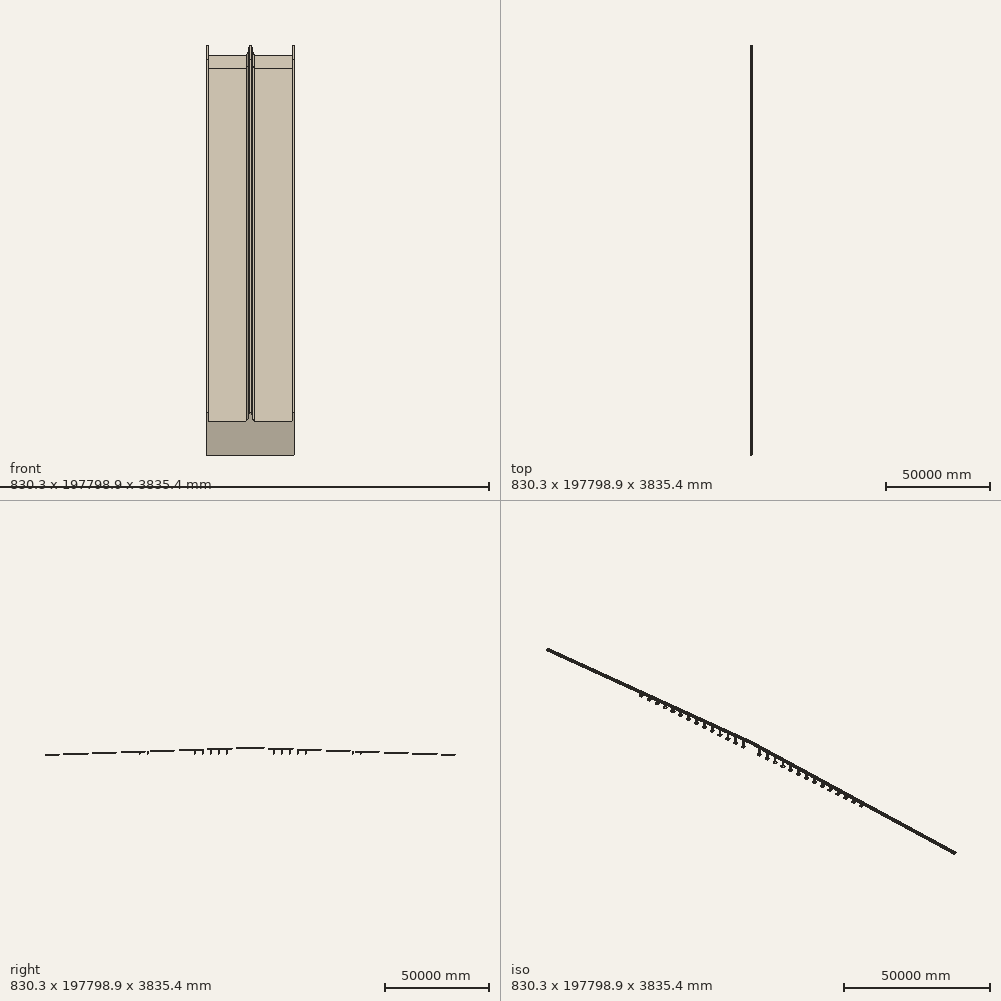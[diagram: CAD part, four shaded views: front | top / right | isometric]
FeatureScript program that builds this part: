
annotation { "Feature Type Name" : "Feature", "Feature Type Description" : "" }
export const myFeature = defineFeature(function(context is Context, id is Id, definition is map)
    precondition{}
    {
        {
            var Q0;
            Q0=qCreatedBy(makeId("Front.planeOp"),FACE);
            var sketch = newSketch(context, id + "F0", { "sketchPlane" : qUnion([Q0])});
            skLineSegment(sketch, "E0", {"start": v(-12.7, 88.9) * mm, "end": v(12.7, 88.9) * mm});
            skLineSegment(sketch, "E1", {"start": v(12.7, 88.9) * mm, "end": v(16.93, 27.52) * mm});
            skLineSegment(sketch, "E2", {"start": v(16.93, 27.52) * mm, "end": v(34.13, 6.35) * mm});
            skLineSegment(sketch, "E3", {"start": v(34.13, 6.35) * mm, "end": v(34.13, 0) * mm});
            skPoint(sketch, "E4", {"position": v(0, 88.9) * mm});
            skLineSegment(sketch, "E5", {"start": v(0, 0) * mm, "end": v(0, 88.9) * mm, "construction": true});
            skLineSegment(sketch, "E6.MirrorCS", {"start": v(-12.7, 88.9) * mm, "end": v(-16.93, 27.52) * mm});
            skLineSegment(sketch, "E7.MirrorCS", {"start": v(-16.93, 27.52) * mm, "end": v(-34.13, 6.35) * mm});
            skLineSegment(sketch, "E8.MirrorCS", {"start": v(-34.13, 6.35) * mm, "end": v(-34.13, 0) * mm});
            skLineSegment(sketch, "E9", {"start": v(34.13, 0) * mm, "end": v(389.73, 0) * mm});
            skLineSegment(sketch, "E10", {"start": v(389.73, 0) * mm, "end": v(389.73, 88.9) * mm});
            skLineSegment(sketch, "E11", {"start": v(389.73, 88.9) * mm, "end": v(415.13, 88.9) * mm});
            skLineSegment(sketch, "E12", {"start": v(415.13, 88.9) * mm, "end": v(415.13, -317.5) * mm});
            skLineSegment(sketch, "E13.MirrorCS", {"start": v(-34.13, 0) * mm, "end": v(-389.73, 0) * mm});
            skLineSegment(sketch, "E14.MirrorCS", {"start": v(-389.73, 0) * mm, "end": v(-389.73, 88.9) * mm});
            skLineSegment(sketch, "E15.MirrorCS", {"start": v(-389.73, 88.9) * mm, "end": v(-415.13, 88.9) * mm});
            skLineSegment(sketch, "E16.MirrorCS", {"start": v(-415.13, 88.9) * mm, "end": v(-415.13, -317.5) * mm});
            skLineSegment(sketch, "E17", {"start": v(-415.13, -317.5) * mm, "end": v(415.13, -317.5) * mm});
            skSolve(sketch);
        }
        {
            var Q0;
            Q0=qCreatedBy(makeId("Right.planeOp"),FACE);
            var sketch = newSketch(context, id + "F1", { "sketchPlane" : qUnion([Q0])});
            skLineSegment(sketch, "E18", {"start": v(0, -317.5) * mm, "end": v(0, -3746.5) * mm, "construction": true});
            skLineSegment(sketch, "E19", {"start": v(-98885.1, -3746.5) * mm, "end": v(-3628.85, -443.34) * mm});
            skPoint(sketch, "E20.visualSharp", {"position": v(0, -317.5) * mm});
            skArc(sketch, "E21", {"start": v(0, -317.5) * mm, "mid": v(-1815.54, -348.33) * mm, "end": v(-3628.85, -443.34) * mm});
            skSolve(sketch);
        }
        {
            var Q0;
            Q0 = qSketchRegion(id + "F0", true);
            var Q1;
            Q1 = qConstructionFilter(qBodyType(qCreatedBy(id + "F1" ,EDGE), BodyType.WIRE), ConstructionObject.NO);
            sweep(context, id + "F2", {"profiles" : qUnion([Q0]), "path" : qUnion([Q1])});
        }
        {
            var Q0;
            Q0=makeQuery(id+"F2.opSweep","SWEPT_BODY",BODY,{"disambiguationData":[OSD([sQuery(id+"F0.wireOp",EDGE,"E0"),sQuery(id+"F0.wireOp",EDGE,"E1"),sQuery(id+"F0.wireOp",EDGE,"E2"),sQuery(id+"F0.wireOp",EDGE,"E3"),sQuery(id+"F0.wireOp",EDGE,"E6.MirrorCS"),sQuery(id+"F0.wireOp",EDGE,"E7.MirrorCS"),sQuery(id+"F0.wireOp",EDGE,"E8.MirrorCS"),sQuery(id+"F0.wireOp",EDGE,"E9"),sQuery(id+"F0.wireOp",EDGE,"E10"),sQuery(id+"F0.wireOp",EDGE,"E11"),sQuery(id+"F0.wireOp",EDGE,"E12"),sQuery(id+"F0.wireOp",EDGE,"E13.MirrorCS"),sQuery(id+"F0.wireOp",EDGE,"E14.MirrorCS"),sQuery(id+"F0.wireOp",EDGE,"E15.MirrorCS"),sQuery(id+"F0.wireOp",EDGE,"E16.MirrorCS"),sQuery(id+"F0.wireOp",EDGE,"E17"),sQuery(id+"F1.wireOp",EDGE,"E21")])]});
            var Q1;
            Q1=qCreatedBy(makeId("Front.planeOp"),FACE);
            mirror(context, id + "F3", {"operationType" : NewBodyOperationType.ADD, "entities" : qUnion([Q0]), "mirrorPlane" : qUnion([Q1])});
        }
        {
            var Q0;
            Q0=qCreatedBy(makeId("Top.planeOp"),FACE);
            cPlane(context, id + "F4", {"entities" : qUnion([Q0]), "cplaneType" : CPlaneType.OFFSET, "offset" : 3429 * mm, "oppositeDirection" : true, "width" : 152.4 * mm, "height" : 152.4 * mm});
        }
        {
            var Q0;
            Q0=qCreatedBy(id+"F4.planeOp",FACE);
            var sketch = newSketch(context, id + "F5", { "sketchPlane" : qUnion([Q0])});
            skLineSegment(sketch, "E22.bottom", {"start": v(-415.13, 3175) * mm, "end": v(415.13, 3175) * mm});
            skLineSegment(sketch, "E22.top", {"start": v(-415.13, 4445) * mm, "end": v(415.13, 4445) * mm});
            skLineSegment(sketch, "E22.left", {"start": v(-415.13, 3175) * mm, "end": v(-415.13, 4445) * mm});
            skLineSegment(sketch, "E22.right", {"start": v(415.13, 3175) * mm, "end": v(415.13, 4445) * mm});
            skLineSegment(sketch, "E23.0.1.0", {"start": v(415.13, 6985) * mm, "end": v(415.13, 8255) * mm});
            skLineSegment(sketch, "E23.0.1.1", {"start": v(-415.13, 6985) * mm, "end": v(-415.13, 8255) * mm});
            skLineSegment(sketch, "E23.0.1.2", {"start": v(-415.13, 8255) * mm, "end": v(415.13, 8255) * mm});
            skLineSegment(sketch, "E23.0.1.3", {"start": v(-415.13, 6985) * mm, "end": v(415.13, 6985) * mm});
            skLineSegment(sketch, "E23.0.2.0", {"start": v(415.13, 10795) * mm, "end": v(415.13, 12065) * mm});
            skLineSegment(sketch, "E23.0.2.1", {"start": v(-415.13, 10795) * mm, "end": v(-415.13, 12065) * mm});
            skLineSegment(sketch, "E23.0.2.2", {"start": v(-415.13, 12065) * mm, "end": v(415.13, 12065) * mm});
            skLineSegment(sketch, "E23.0.2.3", {"start": v(-415.13, 10795) * mm, "end": v(415.13, 10795) * mm});
            skLineSegment(sketch, "E23.0.3.0", {"start": v(415.13, 14605) * mm, "end": v(415.13, 15875) * mm});
            skLineSegment(sketch, "E23.0.3.1", {"start": v(-415.13, 14605) * mm, "end": v(-415.13, 15875) * mm});
            skLineSegment(sketch, "E23.0.3.2", {"start": v(-415.13, 15875) * mm, "end": v(415.13, 15875) * mm});
            skLineSegment(sketch, "E23.0.3.3", {"start": v(-415.13, 14605) * mm, "end": v(415.13, 14605) * mm});
            skLineSegment(sketch, "E23.0.4.0", {"start": v(415.13, 18415) * mm, "end": v(415.13, 19685) * mm});
            skLineSegment(sketch, "E23.0.4.1", {"start": v(-415.13, 18415) * mm, "end": v(-415.13, 19685) * mm});
            skLineSegment(sketch, "E23.0.4.2", {"start": v(-415.13, 19685) * mm, "end": v(415.13, 19685) * mm});
            skLineSegment(sketch, "E23.0.4.3", {"start": v(-415.13, 18415) * mm, "end": v(415.13, 18415) * mm});
            skLineSegment(sketch, "E23.0.5.0", {"start": v(415.13, 22225) * mm, "end": v(415.13, 23495) * mm});
            skLineSegment(sketch, "E23.0.5.1", {"start": v(-415.13, 22225) * mm, "end": v(-415.13, 23495) * mm});
            skLineSegment(sketch, "E23.0.5.2", {"start": v(-415.13, 23495) * mm, "end": v(415.13, 23495) * mm});
            skLineSegment(sketch, "E23.0.5.3", {"start": v(-415.13, 22225) * mm, "end": v(415.13, 22225) * mm});
            skLineSegment(sketch, "E23.0.6.0", {"start": v(415.13, 26035) * mm, "end": v(415.13, 27305) * mm});
            skLineSegment(sketch, "E23.0.6.1", {"start": v(-415.13, 26035) * mm, "end": v(-415.13, 27305) * mm});
            skLineSegment(sketch, "E23.0.6.2", {"start": v(-415.13, 27305) * mm, "end": v(415.13, 27305) * mm});
            skLineSegment(sketch, "E23.0.6.3", {"start": v(-415.13, 26035) * mm, "end": v(415.13, 26035) * mm});
            skLineSegment(sketch, "E23.0.7.0", {"start": v(415.13, 29845) * mm, "end": v(415.13, 31115) * mm});
            skLineSegment(sketch, "E23.0.7.1", {"start": v(-415.13, 29845) * mm, "end": v(-415.13, 31115) * mm});
            skLineSegment(sketch, "E23.0.7.2", {"start": v(-415.13, 31115) * mm, "end": v(415.13, 31115) * mm});
            skLineSegment(sketch, "E23.0.7.3", {"start": v(-415.13, 29845) * mm, "end": v(415.13, 29845) * mm});
            skLineSegment(sketch, "E23.direction1", {"start": v(-415.13, 3175) * mm, "end": v(-389.73, 3175) * mm, "construction": true});
            skLineSegment(sketch, "E23.direction2", {"start": v(-415.13, 3175) * mm, "end": v(-415.13, 6985) * mm, "construction": true});
            skLineSegment(sketch, "E24.0.0.8", {"start": v(415.13, 33655) * mm, "end": v(415.13, 34925) * mm});
            skLineSegment(sketch, "E24.3.0.8", {"start": v(-415.13, 33655) * mm, "end": v(-415.13, 34925) * mm});
            skLineSegment(sketch, "E24.6.0.8", {"start": v(-415.13, 34925) * mm, "end": v(415.13, 34925) * mm});
            skLineSegment(sketch, "E24.9.0.8", {"start": v(-415.13, 33655) * mm, "end": v(415.13, 33655) * mm});
            skLineSegment(sketch, "E24.0.0.9", {"start": v(415.13, 37465) * mm, "end": v(415.13, 38735) * mm});
            skLineSegment(sketch, "E24.3.0.9", {"start": v(-415.13, 37465) * mm, "end": v(-415.13, 38735) * mm});
            skLineSegment(sketch, "E24.6.0.9", {"start": v(-415.13, 38735) * mm, "end": v(415.13, 38735) * mm});
            skLineSegment(sketch, "E24.9.0.9", {"start": v(-415.13, 37465) * mm, "end": v(415.13, 37465) * mm});
            skLineSegment(sketch, "E24.0.0.10", {"start": v(415.13, 41275) * mm, "end": v(415.13, 42545) * mm});
            skLineSegment(sketch, "E24.3.0.10", {"start": v(-415.13, 41275) * mm, "end": v(-415.13, 42545) * mm});
            skLineSegment(sketch, "E24.6.0.10", {"start": v(-415.13, 42545) * mm, "end": v(415.13, 42545) * mm});
            skLineSegment(sketch, "E24.9.0.10", {"start": v(-415.13, 41275) * mm, "end": v(415.13, 41275) * mm});
            skLineSegment(sketch, "E24.0.0.11", {"start": v(415.13, 45085) * mm, "end": v(415.13, 46355) * mm});
            skLineSegment(sketch, "E24.3.0.11", {"start": v(-415.13, 45085) * mm, "end": v(-415.13, 46355) * mm});
            skLineSegment(sketch, "E24.6.0.11", {"start": v(-415.13, 46355) * mm, "end": v(415.13, 46355) * mm});
            skLineSegment(sketch, "E24.9.0.11", {"start": v(-415.13, 45085) * mm, "end": v(415.13, 45085) * mm});
            skLineSegment(sketch, "E24.0.0.12", {"start": v(415.13, 48895) * mm, "end": v(415.13, 50165) * mm});
            skLineSegment(sketch, "E24.3.0.12", {"start": v(-415.13, 48895) * mm, "end": v(-415.13, 50165) * mm});
            skLineSegment(sketch, "E24.6.0.12", {"start": v(-415.13, 50165) * mm, "end": v(415.13, 50165) * mm});
            skLineSegment(sketch, "E24.9.0.12", {"start": v(-415.13, 48895) * mm, "end": v(415.13, 48895) * mm});
            skLineSegment(sketch, "E24.0.0.13", {"start": v(415.13, 52705) * mm, "end": v(415.13, 53975) * mm});
            skLineSegment(sketch, "E24.3.0.13", {"start": v(-415.13, 52705) * mm, "end": v(-415.13, 53975) * mm});
            skLineSegment(sketch, "E24.6.0.13", {"start": v(-415.13, 53975) * mm, "end": v(415.13, 53975) * mm});
            skLineSegment(sketch, "E24.9.0.13", {"start": v(-415.13, 52705) * mm, "end": v(415.13, 52705) * mm});
            skLineSegment(sketch, "E25", {"start": v(-1571.05, 0) * mm, "end": v(1415.11, 0) * mm, "construction": true});
            skLineSegment(sketch, "E26.MirrorCS", {"start": v(-415.13, -3175) * mm, "end": v(415.13, -3175) * mm});
            skLineSegment(sketch, "E27.MirrorCS", {"start": v(-415.13, -3175) * mm, "end": v(-389.73, -3175) * mm, "construction": true});
            skLineSegment(sketch, "E28.MirrorCS", {"start": v(415.13, -6985) * mm, "end": v(415.13, -8255) * mm});
            skLineSegment(sketch, "E29.MirrorCS", {"start": v(-415.13, -6985) * mm, "end": v(-415.13, -8255) * mm});
            skLineSegment(sketch, "E30.MirrorCS", {"start": v(-415.13, -6985) * mm, "end": v(415.13, -6985) * mm});
            skLineSegment(sketch, "E31.MirrorCS", {"start": v(415.13, -52705) * mm, "end": v(415.13, -53975) * mm});
            skLineSegment(sketch, "E32.MirrorCS", {"start": v(-415.13, -19685) * mm, "end": v(415.13, -19685) * mm});
            skLineSegment(sketch, "E33.MirrorCS", {"start": v(415.13, -33655) * mm, "end": v(415.13, -34925) * mm});
            skLineSegment(sketch, "E34.MirrorCS", {"start": v(-415.13, -26035) * mm, "end": v(-415.13, -27305) * mm});
            skLineSegment(sketch, "E35.MirrorCS", {"start": v(-415.13, -37465) * mm, "end": v(415.13, -37465) * mm});
            skLineSegment(sketch, "E36.MirrorCS", {"start": v(-415.13, -52705) * mm, "end": v(415.13, -52705) * mm});
            skLineSegment(sketch, "E37.MirrorCS", {"start": v(-415.13, -18415) * mm, "end": v(-415.13, -19685) * mm});
            skLineSegment(sketch, "E38.MirrorCS", {"start": v(-415.13, -3175) * mm, "end": v(-415.13, -6985) * mm, "construction": true});
            skLineSegment(sketch, "E39.MirrorCS", {"start": v(-415.13, -45085) * mm, "end": v(-415.13, -46355) * mm});
            skLineSegment(sketch, "E40.MirrorCS", {"start": v(-415.13, -23495) * mm, "end": v(415.13, -23495) * mm});
            skLineSegment(sketch, "E41.MirrorCS", {"start": v(415.13, -26035) * mm, "end": v(415.13, -27305) * mm});
            skLineSegment(sketch, "E42.MirrorCS", {"start": v(-415.13, -38735) * mm, "end": v(415.13, -38735) * mm});
            skLineSegment(sketch, "E43.MirrorCS", {"start": v(-415.13, -53975) * mm, "end": v(415.13, -53975) * mm});
            skLineSegment(sketch, "E44.MirrorCS", {"start": v(-415.13, -45085) * mm, "end": v(415.13, -45085) * mm});
            skLineSegment(sketch, "E45.MirrorCS", {"start": v(-415.13, -22225) * mm, "end": v(415.13, -22225) * mm});
            skLineSegment(sketch, "E46.MirrorCS", {"start": v(-415.13, -37465) * mm, "end": v(-415.13, -38735) * mm});
            skLineSegment(sketch, "E47.MirrorCS", {"start": v(-415.13, -52705) * mm, "end": v(-415.13, -53975) * mm});
            skLineSegment(sketch, "E48.MirrorCS", {"start": v(-415.13, -29845) * mm, "end": v(415.13, -29845) * mm});
            skLineSegment(sketch, "E49.MirrorCS", {"start": v(415.13, -37465) * mm, "end": v(415.13, -38735) * mm});
            skLineSegment(sketch, "E50.MirrorCS", {"start": v(-415.13, -48895) * mm, "end": v(415.13, -48895) * mm});
            skLineSegment(sketch, "E51.MirrorCS", {"start": v(415.13, -45085) * mm, "end": v(415.13, -46355) * mm});
            skLineSegment(sketch, "E52.MirrorCS", {"start": v(-415.13, -22225) * mm, "end": v(-415.13, -23495) * mm});
            skLineSegment(sketch, "E53.MirrorCS", {"start": v(-415.13, -31115) * mm, "end": v(415.13, -31115) * mm});
            skLineSegment(sketch, "E54.MirrorCS", {"start": v(-415.13, -33655) * mm, "end": v(415.13, -33655) * mm});
            skLineSegment(sketch, "E55.MirrorCS", {"start": v(415.13, -14605) * mm, "end": v(415.13, -15875) * mm});
            skLineSegment(sketch, "E56.MirrorCS", {"start": v(-415.13, -10795) * mm, "end": v(415.13, -10795) * mm});
            skLineSegment(sketch, "E57.MirrorCS", {"start": v(415.13, -48895) * mm, "end": v(415.13, -50165) * mm});
            skLineSegment(sketch, "E58.MirrorCS", {"start": v(-415.13, -4445) * mm, "end": v(415.13, -4445) * mm});
            skLineSegment(sketch, "E59.MirrorCS", {"start": v(415.13, -22225) * mm, "end": v(415.13, -23495) * mm});
            skLineSegment(sketch, "E60.MirrorCS", {"start": v(-415.13, -34925) * mm, "end": v(415.13, -34925) * mm});
            skLineSegment(sketch, "E61.MirrorCS", {"start": v(-415.13, -14605) * mm, "end": v(415.13, -14605) * mm});
            skLineSegment(sketch, "E62.MirrorCS", {"start": v(-415.13, -18415) * mm, "end": v(415.13, -18415) * mm});
            skLineSegment(sketch, "E63.MirrorCS", {"start": v(-415.13, -3175) * mm, "end": v(-415.13, -4445) * mm});
            skLineSegment(sketch, "E64.MirrorCS", {"start": v(415.13, -3175) * mm, "end": v(415.13, -4445) * mm});
            skLineSegment(sketch, "E65.MirrorCS", {"start": v(-415.13, -48895) * mm, "end": v(-415.13, -50165) * mm});
            skLineSegment(sketch, "E66.MirrorCS", {"start": v(-415.13, -15875) * mm, "end": v(415.13, -15875) * mm});
            skLineSegment(sketch, "E67.MirrorCS", {"start": v(-415.13, -46355) * mm, "end": v(415.13, -46355) * mm});
            skLineSegment(sketch, "E68.MirrorCS", {"start": v(-415.13, -12065) * mm, "end": v(415.13, -12065) * mm});
            skLineSegment(sketch, "E69.MirrorCS", {"start": v(-415.13, -33655) * mm, "end": v(-415.13, -34925) * mm});
            skLineSegment(sketch, "E70.MirrorCS", {"start": v(-415.13, -42545) * mm, "end": v(415.13, -42545) * mm});
            skLineSegment(sketch, "E71.MirrorCS", {"start": v(415.13, -29845) * mm, "end": v(415.13, -31115) * mm});
            skLineSegment(sketch, "E72.MirrorCS", {"start": v(415.13, -41275) * mm, "end": v(415.13, -42545) * mm});
            skLineSegment(sketch, "E73.MirrorCS", {"start": v(-415.13, -27305) * mm, "end": v(415.13, -27305) * mm});
            skLineSegment(sketch, "E74.MirrorCS", {"start": v(-415.13, -29845) * mm, "end": v(-415.13, -31115) * mm});
            skLineSegment(sketch, "E75.MirrorCS", {"start": v(-415.13, -26035) * mm, "end": v(415.13, -26035) * mm});
            skLineSegment(sketch, "E76.MirrorCS", {"start": v(-415.13, -41275) * mm, "end": v(-415.13, -42545) * mm});
            skLineSegment(sketch, "E77.MirrorCS", {"start": v(-415.13, -14605) * mm, "end": v(-415.13, -15875) * mm});
            skLineSegment(sketch, "E78.MirrorCS", {"start": v(-415.13, -50165) * mm, "end": v(415.13, -50165) * mm});
            skLineSegment(sketch, "E79.MirrorCS", {"start": v(-415.13, -8255) * mm, "end": v(415.13, -8255) * mm});
            skLineSegment(sketch, "E80.MirrorCS", {"start": v(-415.13, -41275) * mm, "end": v(415.13, -41275) * mm});
            skLineSegment(sketch, "E81.MirrorCS", {"start": v(415.13, -18415) * mm, "end": v(415.13, -19685) * mm});
            skLineSegment(sketch, "E82.MirrorCS", {"start": v(415.13, -10795) * mm, "end": v(415.13, -12065) * mm});
            skLineSegment(sketch, "E83.MirrorCS", {"start": v(-415.13, -10795) * mm, "end": v(-415.13, -12065) * mm});
            skSolve(sketch);
        }
        {
            var Q0;
            Q0 = qSketchRegion(id + "F5", true);
            extrude(context, id + "F6", {"entities" : qUnion([Q0]), "depth" : 254 * mm});
        }
        {
            var Q0;
            Q0=makeQuery(id+"F6.opExtrude","CAP_FACE",FACE,{"disambiguationData":[OSD([sQuery(id+"F5.wireOp",EDGE,"E22.bottom"),sQuery(id+"F5.wireOp",EDGE,"E22.top"),sQuery(id+"F5.wireOp",EDGE,"E22.left"),sQuery(id+"F5.wireOp",EDGE,"E22.right")])],"isStart":false});
            var sketch = newSketch(context, id + "F7", { "sketchPlane" : qUnion([Q0])});
            skLineSegment(sketch, "E84.bottom", {"start": v(-310.16, 3937) * mm, "end": v(-183.16, 3937) * mm});
            skLineSegment(sketch, "E84.top", {"start": v(-310.16, 3683) * mm, "end": v(-183.16, 3683) * mm});
            skLineSegment(sketch, "E84.left", {"start": v(-310.16, 3937) * mm, "end": v(-310.16, 3683) * mm});
            skPoint(sketch, "E85", {"position": v(-415.13, 3810) * mm});
            skPoint(sketch, "E86.positionSnap0", {"position": v(-310.16, 3810) * mm});
            skPoint(sketch, "E87", {"position": v(0, 3175) * mm});
            skLineSegment(sketch, "E88", {"start": v(-183.16, 3937) * mm, "end": v(-183.16, 3879.85) * mm});
            skLineSegment(sketch, "E89", {"start": v(-183.16, 3879.85) * mm, "end": v(183.16, 3879.85) * mm});
            skLineSegment(sketch, "E90", {"start": v(183.16, 3879.85) * mm, "end": v(183.16, 3937) * mm});
            skLineSegment(sketch, "E91", {"start": v(183.16, 3937) * mm, "end": v(310.16, 3937) * mm});
            skLineSegment(sketch, "E92", {"start": v(310.16, 3937) * mm, "end": v(310.16, 3683) * mm});
            skLineSegment(sketch, "E93", {"start": v(310.16, 3683) * mm, "end": v(183.16, 3683) * mm});
            skLineSegment(sketch, "E94", {"start": v(183.16, 3683) * mm, "end": v(183.16, 3740.15) * mm});
            skLineSegment(sketch, "E95", {"start": v(183.16, 3740.15) * mm, "end": v(-183.16, 3740.15) * mm});
            skLineSegment(sketch, "E96", {"start": v(-183.16, 3740.15) * mm, "end": v(-183.16, 3683) * mm});
            skPoint(sketch, "E97", {"position": v(0, 3740.15) * mm});
            skPoint(sketch, "E98.0.1.0", {"position": v(-415.13, 7620) * mm});
            skLineSegment(sketch, "E98.0.1.1", {"start": v(183.16, 7550.15) * mm, "end": v(-183.16, 7550.15) * mm});
            skPoint(sketch, "E98.0.1.2", {"position": v(-310.16, 7620) * mm});
            skPoint(sketch, "E98.0.1.3", {"position": v(0, 7550.15) * mm});
            skLineSegment(sketch, "E98.0.1.4", {"start": v(310.16, 7747) * mm, "end": v(310.16, 7493) * mm});
            skLineSegment(sketch, "E98.0.1.5", {"start": v(-183.16, 7689.85) * mm, "end": v(183.16, 7689.85) * mm});
            skLineSegment(sketch, "E98.0.1.6", {"start": v(-310.16, 7747) * mm, "end": v(-310.16, 7493) * mm});
            skLineSegment(sketch, "E98.0.1.7", {"start": v(-183.16, 7747) * mm, "end": v(-183.16, 7689.85) * mm});
            skLineSegment(sketch, "E98.0.1.8", {"start": v(183.16, 7493) * mm, "end": v(183.16, 7550.15) * mm});
            skLineSegment(sketch, "E98.0.1.9", {"start": v(-183.16, 7550.15) * mm, "end": v(-183.16, 7493) * mm});
            skLineSegment(sketch, "E98.0.1.10", {"start": v(-310.16, 7493) * mm, "end": v(-183.16, 7493) * mm});
            skLineSegment(sketch, "E98.0.1.11", {"start": v(-310.16, 7747) * mm, "end": v(-183.16, 7747) * mm});
            skLineSegment(sketch, "E98.0.1.12", {"start": v(183.16, 7689.85) * mm, "end": v(183.16, 7747) * mm});
            skLineSegment(sketch, "E98.0.1.13", {"start": v(183.16, 7747) * mm, "end": v(310.16, 7747) * mm});
            skLineSegment(sketch, "E98.0.1.14", {"start": v(310.16, 7493) * mm, "end": v(183.16, 7493) * mm});
            skPoint(sketch, "E98.0.2.0", {"position": v(-415.13, 11430) * mm});
            skLineSegment(sketch, "E98.0.2.1", {"start": v(183.16, 11360.15) * mm, "end": v(-183.16, 11360.15) * mm});
            skPoint(sketch, "E98.0.2.2", {"position": v(-310.16, 11430) * mm});
            skPoint(sketch, "E98.0.2.3", {"position": v(0, 11360.15) * mm});
            skLineSegment(sketch, "E98.0.2.4", {"start": v(310.16, 11557) * mm, "end": v(310.16, 11303) * mm});
            skLineSegment(sketch, "E98.0.2.5", {"start": v(-183.16, 11499.85) * mm, "end": v(183.16, 11499.85) * mm});
            skLineSegment(sketch, "E98.0.2.6", {"start": v(-310.16, 11557) * mm, "end": v(-310.16, 11303) * mm});
            skLineSegment(sketch, "E98.0.2.7", {"start": v(-183.16, 11557) * mm, "end": v(-183.16, 11499.85) * mm});
            skLineSegment(sketch, "E98.0.2.8", {"start": v(183.16, 11303) * mm, "end": v(183.16, 11360.15) * mm});
            skLineSegment(sketch, "E98.0.2.9", {"start": v(-183.16, 11360.15) * mm, "end": v(-183.16, 11303) * mm});
            skLineSegment(sketch, "E98.0.2.10", {"start": v(-310.16, 11303) * mm, "end": v(-183.16, 11303) * mm});
            skLineSegment(sketch, "E98.0.2.11", {"start": v(-310.16, 11557) * mm, "end": v(-183.16, 11557) * mm});
            skLineSegment(sketch, "E98.0.2.12", {"start": v(183.16, 11499.85) * mm, "end": v(183.16, 11557) * mm});
            skLineSegment(sketch, "E98.0.2.13", {"start": v(183.16, 11557) * mm, "end": v(310.16, 11557) * mm});
            skLineSegment(sketch, "E98.0.2.14", {"start": v(310.16, 11303) * mm, "end": v(183.16, 11303) * mm});
            skPoint(sketch, "E98.0.3.0", {"position": v(-415.13, 15240) * mm});
            skLineSegment(sketch, "E98.0.3.1", {"start": v(183.16, 15170.15) * mm, "end": v(-183.16, 15170.15) * mm});
            skPoint(sketch, "E98.0.3.2", {"position": v(-310.16, 15240) * mm});
            skPoint(sketch, "E98.0.3.3", {"position": v(0, 15170.15) * mm});
            skLineSegment(sketch, "E98.0.3.4", {"start": v(310.16, 15367) * mm, "end": v(310.16, 15113) * mm});
            skLineSegment(sketch, "E98.0.3.5", {"start": v(-183.16, 15309.85) * mm, "end": v(183.16, 15309.85) * mm});
            skLineSegment(sketch, "E98.0.3.6", {"start": v(-310.16, 15367) * mm, "end": v(-310.16, 15113) * mm});
            skLineSegment(sketch, "E98.0.3.7", {"start": v(-183.16, 15367) * mm, "end": v(-183.16, 15309.85) * mm});
            skLineSegment(sketch, "E98.0.3.8", {"start": v(183.16, 15113) * mm, "end": v(183.16, 15170.15) * mm});
            skLineSegment(sketch, "E98.0.3.9", {"start": v(-183.16, 15170.15) * mm, "end": v(-183.16, 15113) * mm});
            skLineSegment(sketch, "E98.0.3.10", {"start": v(-310.16, 15113) * mm, "end": v(-183.16, 15113) * mm});
            skLineSegment(sketch, "E98.0.3.11", {"start": v(-310.16, 15367) * mm, "end": v(-183.16, 15367) * mm});
            skLineSegment(sketch, "E98.0.3.12", {"start": v(183.16, 15309.85) * mm, "end": v(183.16, 15367) * mm});
            skLineSegment(sketch, "E98.0.3.13", {"start": v(183.16, 15367) * mm, "end": v(310.16, 15367) * mm});
            skLineSegment(sketch, "E98.0.3.14", {"start": v(310.16, 15113) * mm, "end": v(183.16, 15113) * mm});
            skPoint(sketch, "E98.0.4.0", {"position": v(-415.13, 19050) * mm});
            skLineSegment(sketch, "E98.0.4.1", {"start": v(183.16, 18980.15) * mm, "end": v(-183.16, 18980.15) * mm});
            skPoint(sketch, "E98.0.4.2", {"position": v(-310.16, 19050) * mm});
            skPoint(sketch, "E98.0.4.3", {"position": v(0, 18980.15) * mm});
            skLineSegment(sketch, "E98.0.4.4", {"start": v(310.16, 19177) * mm, "end": v(310.16, 18923) * mm});
            skLineSegment(sketch, "E98.0.4.5", {"start": v(-183.16, 19119.85) * mm, "end": v(183.16, 19119.85) * mm});
            skLineSegment(sketch, "E98.0.4.6", {"start": v(-310.16, 19177) * mm, "end": v(-310.16, 18923) * mm});
            skLineSegment(sketch, "E98.0.4.7", {"start": v(-183.16, 19177) * mm, "end": v(-183.16, 19119.85) * mm});
            skLineSegment(sketch, "E98.0.4.8", {"start": v(183.16, 18923) * mm, "end": v(183.16, 18980.15) * mm});
            skLineSegment(sketch, "E98.0.4.9", {"start": v(-183.16, 18980.15) * mm, "end": v(-183.16, 18923) * mm});
            skLineSegment(sketch, "E98.0.4.10", {"start": v(-310.16, 18923) * mm, "end": v(-183.16, 18923) * mm});
            skLineSegment(sketch, "E98.0.4.11", {"start": v(-310.16, 19177) * mm, "end": v(-183.16, 19177) * mm});
            skLineSegment(sketch, "E98.0.4.12", {"start": v(183.16, 19119.85) * mm, "end": v(183.16, 19177) * mm});
            skLineSegment(sketch, "E98.0.4.13", {"start": v(183.16, 19177) * mm, "end": v(310.16, 19177) * mm});
            skLineSegment(sketch, "E98.0.4.14", {"start": v(310.16, 18923) * mm, "end": v(183.16, 18923) * mm});
            skPoint(sketch, "E98.0.5.0", {"position": v(-415.13, 22860) * mm});
            skLineSegment(sketch, "E98.0.5.1", {"start": v(183.16, 22790.15) * mm, "end": v(-183.16, 22790.15) * mm});
            skPoint(sketch, "E98.0.5.2", {"position": v(-310.16, 22860) * mm});
            skPoint(sketch, "E98.0.5.3", {"position": v(0, 22790.15) * mm});
            skLineSegment(sketch, "E98.0.5.4", {"start": v(310.16, 22987) * mm, "end": v(310.16, 22733) * mm});
            skLineSegment(sketch, "E98.0.5.5", {"start": v(-183.16, 22929.85) * mm, "end": v(183.16, 22929.85) * mm});
            skLineSegment(sketch, "E98.0.5.6", {"start": v(-310.16, 22987) * mm, "end": v(-310.16, 22733) * mm});
            skLineSegment(sketch, "E98.0.5.7", {"start": v(-183.16, 22987) * mm, "end": v(-183.16, 22929.85) * mm});
            skLineSegment(sketch, "E98.0.5.8", {"start": v(183.16, 22733) * mm, "end": v(183.16, 22790.15) * mm});
            skLineSegment(sketch, "E98.0.5.9", {"start": v(-183.16, 22790.15) * mm, "end": v(-183.16, 22733) * mm});
            skLineSegment(sketch, "E98.0.5.10", {"start": v(-310.16, 22733) * mm, "end": v(-183.16, 22733) * mm});
            skLineSegment(sketch, "E98.0.5.11", {"start": v(-310.16, 22987) * mm, "end": v(-183.16, 22987) * mm});
            skLineSegment(sketch, "E98.0.5.12", {"start": v(183.16, 22929.85) * mm, "end": v(183.16, 22987) * mm});
            skLineSegment(sketch, "E98.0.5.13", {"start": v(183.16, 22987) * mm, "end": v(310.16, 22987) * mm});
            skLineSegment(sketch, "E98.0.5.14", {"start": v(310.16, 22733) * mm, "end": v(183.16, 22733) * mm});
            skPoint(sketch, "E98.0.6.0", {"position": v(-415.13, 26670) * mm});
            skLineSegment(sketch, "E98.0.6.1", {"start": v(183.16, 26600.15) * mm, "end": v(-183.16, 26600.15) * mm});
            skPoint(sketch, "E98.0.6.2", {"position": v(-310.16, 26670) * mm});
            skPoint(sketch, "E98.0.6.3", {"position": v(0, 26600.15) * mm});
            skLineSegment(sketch, "E98.0.6.4", {"start": v(310.16, 26797) * mm, "end": v(310.16, 26543) * mm});
            skLineSegment(sketch, "E98.0.6.5", {"start": v(-183.16, 26739.85) * mm, "end": v(183.16, 26739.85) * mm});
            skLineSegment(sketch, "E98.0.6.6", {"start": v(-310.16, 26797) * mm, "end": v(-310.16, 26543) * mm});
            skLineSegment(sketch, "E98.0.6.7", {"start": v(-183.16, 26797) * mm, "end": v(-183.16, 26739.85) * mm});
            skLineSegment(sketch, "E98.0.6.8", {"start": v(183.16, 26543) * mm, "end": v(183.16, 26600.15) * mm});
            skLineSegment(sketch, "E98.0.6.9", {"start": v(-183.16, 26600.15) * mm, "end": v(-183.16, 26543) * mm});
            skLineSegment(sketch, "E98.0.6.10", {"start": v(-310.16, 26543) * mm, "end": v(-183.16, 26543) * mm});
            skLineSegment(sketch, "E98.0.6.11", {"start": v(-310.16, 26797) * mm, "end": v(-183.16, 26797) * mm});
            skLineSegment(sketch, "E98.0.6.12", {"start": v(183.16, 26739.85) * mm, "end": v(183.16, 26797) * mm});
            skLineSegment(sketch, "E98.0.6.13", {"start": v(183.16, 26797) * mm, "end": v(310.16, 26797) * mm});
            skLineSegment(sketch, "E98.0.6.14", {"start": v(310.16, 26543) * mm, "end": v(183.16, 26543) * mm});
            skPoint(sketch, "E98.0.7.0", {"position": v(-415.13, 30480) * mm});
            skLineSegment(sketch, "E98.0.7.1", {"start": v(183.16, 30410.15) * mm, "end": v(-183.16, 30410.15) * mm});
            skPoint(sketch, "E98.0.7.2", {"position": v(-310.16, 30480) * mm});
            skPoint(sketch, "E98.0.7.3", {"position": v(0, 30410.15) * mm});
            skLineSegment(sketch, "E98.0.7.4", {"start": v(310.16, 30607) * mm, "end": v(310.16, 30353) * mm});
            skLineSegment(sketch, "E98.0.7.5", {"start": v(-183.16, 30549.85) * mm, "end": v(183.16, 30549.85) * mm});
            skLineSegment(sketch, "E98.0.7.6", {"start": v(-310.16, 30607) * mm, "end": v(-310.16, 30353) * mm});
            skLineSegment(sketch, "E98.0.7.7", {"start": v(-183.16, 30607) * mm, "end": v(-183.16, 30549.85) * mm});
            skLineSegment(sketch, "E98.0.7.8", {"start": v(183.16, 30353) * mm, "end": v(183.16, 30410.15) * mm});
            skLineSegment(sketch, "E98.0.7.9", {"start": v(-183.16, 30410.15) * mm, "end": v(-183.16, 30353) * mm});
            skLineSegment(sketch, "E98.0.7.10", {"start": v(-310.16, 30353) * mm, "end": v(-183.16, 30353) * mm});
            skLineSegment(sketch, "E98.0.7.11", {"start": v(-310.16, 30607) * mm, "end": v(-183.16, 30607) * mm});
            skLineSegment(sketch, "E98.0.7.12", {"start": v(183.16, 30549.85) * mm, "end": v(183.16, 30607) * mm});
            skLineSegment(sketch, "E98.0.7.13", {"start": v(183.16, 30607) * mm, "end": v(310.16, 30607) * mm});
            skLineSegment(sketch, "E98.0.7.14", {"start": v(310.16, 30353) * mm, "end": v(183.16, 30353) * mm});
            skPoint(sketch, "E98.0.8.0", {"position": v(-415.13, 34290) * mm});
            skLineSegment(sketch, "E98.0.8.1", {"start": v(183.16, 34220.15) * mm, "end": v(-183.16, 34220.15) * mm});
            skPoint(sketch, "E98.0.8.2", {"position": v(-310.16, 34290) * mm});
            skPoint(sketch, "E98.0.8.3", {"position": v(0, 34220.15) * mm});
            skLineSegment(sketch, "E98.0.8.4", {"start": v(310.16, 34417) * mm, "end": v(310.16, 34163) * mm});
            skLineSegment(sketch, "E98.0.8.5", {"start": v(-183.16, 34359.85) * mm, "end": v(183.16, 34359.85) * mm});
            skLineSegment(sketch, "E98.0.8.6", {"start": v(-310.16, 34417) * mm, "end": v(-310.16, 34163) * mm});
            skLineSegment(sketch, "E98.0.8.7", {"start": v(-183.16, 34417) * mm, "end": v(-183.16, 34359.85) * mm});
            skLineSegment(sketch, "E98.0.8.8", {"start": v(183.16, 34163) * mm, "end": v(183.16, 34220.15) * mm});
            skLineSegment(sketch, "E98.0.8.9", {"start": v(-183.16, 34220.15) * mm, "end": v(-183.16, 34163) * mm});
            skLineSegment(sketch, "E98.0.8.10", {"start": v(-310.16, 34163) * mm, "end": v(-183.16, 34163) * mm});
            skLineSegment(sketch, "E98.0.8.11", {"start": v(-310.16, 34417) * mm, "end": v(-183.16, 34417) * mm});
            skLineSegment(sketch, "E98.0.8.12", {"start": v(183.16, 34359.85) * mm, "end": v(183.16, 34417) * mm});
            skLineSegment(sketch, "E98.0.8.13", {"start": v(183.16, 34417) * mm, "end": v(310.16, 34417) * mm});
            skLineSegment(sketch, "E98.0.8.14", {"start": v(310.16, 34163) * mm, "end": v(183.16, 34163) * mm});
            skPoint(sketch, "E98.0.9.0", {"position": v(-415.13, 38100) * mm});
            skLineSegment(sketch, "E98.0.9.1", {"start": v(183.16, 38030.15) * mm, "end": v(-183.16, 38030.15) * mm});
            skPoint(sketch, "E98.0.9.2", {"position": v(-310.16, 38100) * mm});
            skPoint(sketch, "E98.0.9.3", {"position": v(0, 38030.15) * mm});
            skLineSegment(sketch, "E98.0.9.4", {"start": v(310.16, 38227) * mm, "end": v(310.16, 37973) * mm});
            skLineSegment(sketch, "E98.0.9.5", {"start": v(-183.16, 38169.85) * mm, "end": v(183.16, 38169.85) * mm});
            skLineSegment(sketch, "E98.0.9.6", {"start": v(-310.16, 38227) * mm, "end": v(-310.16, 37973) * mm});
            skLineSegment(sketch, "E98.0.9.7", {"start": v(-183.16, 38227) * mm, "end": v(-183.16, 38169.85) * mm});
            skLineSegment(sketch, "E98.0.9.8", {"start": v(183.16, 37973) * mm, "end": v(183.16, 38030.15) * mm});
            skLineSegment(sketch, "E98.0.9.9", {"start": v(-183.16, 38030.15) * mm, "end": v(-183.16, 37973) * mm});
            skLineSegment(sketch, "E98.0.9.10", {"start": v(-310.16, 37973) * mm, "end": v(-183.16, 37973) * mm});
            skLineSegment(sketch, "E98.0.9.11", {"start": v(-310.16, 38227) * mm, "end": v(-183.16, 38227) * mm});
            skLineSegment(sketch, "E98.0.9.12", {"start": v(183.16, 38169.85) * mm, "end": v(183.16, 38227) * mm});
            skLineSegment(sketch, "E98.0.9.13", {"start": v(183.16, 38227) * mm, "end": v(310.16, 38227) * mm});
            skLineSegment(sketch, "E98.0.9.14", {"start": v(310.16, 37973) * mm, "end": v(183.16, 37973) * mm});
            skPoint(sketch, "E98.0.10.0", {"position": v(-415.13, 41910) * mm});
            skLineSegment(sketch, "E98.0.10.1", {"start": v(183.16, 41840.15) * mm, "end": v(-183.16, 41840.15) * mm});
            skPoint(sketch, "E98.0.10.2", {"position": v(-310.16, 41910) * mm});
            skPoint(sketch, "E98.0.10.3", {"position": v(0, 41840.15) * mm});
            skLineSegment(sketch, "E98.0.10.4", {"start": v(310.16, 42037) * mm, "end": v(310.16, 41783) * mm});
            skLineSegment(sketch, "E98.0.10.5", {"start": v(-183.16, 41979.85) * mm, "end": v(183.16, 41979.85) * mm});
            skLineSegment(sketch, "E98.0.10.6", {"start": v(-310.16, 42037) * mm, "end": v(-310.16, 41783) * mm});
            skLineSegment(sketch, "E98.0.10.7", {"start": v(-183.16, 42037) * mm, "end": v(-183.16, 41979.85) * mm});
            skLineSegment(sketch, "E98.0.10.8", {"start": v(183.16, 41783) * mm, "end": v(183.16, 41840.15) * mm});
            skLineSegment(sketch, "E98.0.10.9", {"start": v(-183.16, 41840.15) * mm, "end": v(-183.16, 41783) * mm});
            skLineSegment(sketch, "E98.0.10.10", {"start": v(-310.16, 41783) * mm, "end": v(-183.16, 41783) * mm});
            skLineSegment(sketch, "E98.0.10.11", {"start": v(-310.16, 42037) * mm, "end": v(-183.16, 42037) * mm});
            skLineSegment(sketch, "E98.0.10.12", {"start": v(183.16, 41979.85) * mm, "end": v(183.16, 42037) * mm});
            skLineSegment(sketch, "E98.0.10.13", {"start": v(183.16, 42037) * mm, "end": v(310.16, 42037) * mm});
            skLineSegment(sketch, "E98.0.10.14", {"start": v(310.16, 41783) * mm, "end": v(183.16, 41783) * mm});
            skPoint(sketch, "E98.0.11.0", {"position": v(-415.13, 45720) * mm});
            skLineSegment(sketch, "E98.0.11.1", {"start": v(183.16, 45650.15) * mm, "end": v(-183.16, 45650.15) * mm});
            skPoint(sketch, "E98.0.11.2", {"position": v(-310.16, 45720) * mm});
            skPoint(sketch, "E98.0.11.3", {"position": v(0, 45650.15) * mm});
            skLineSegment(sketch, "E98.0.11.4", {"start": v(310.16, 45847) * mm, "end": v(310.16, 45593) * mm});
            skLineSegment(sketch, "E98.0.11.5", {"start": v(-183.16, 45789.85) * mm, "end": v(183.16, 45789.85) * mm});
            skLineSegment(sketch, "E98.0.11.6", {"start": v(-310.16, 45847) * mm, "end": v(-310.16, 45593) * mm});
            skLineSegment(sketch, "E98.0.11.7", {"start": v(-183.16, 45847) * mm, "end": v(-183.16, 45789.85) * mm});
            skLineSegment(sketch, "E98.0.11.8", {"start": v(183.16, 45593) * mm, "end": v(183.16, 45650.15) * mm});
            skLineSegment(sketch, "E98.0.11.9", {"start": v(-183.16, 45650.15) * mm, "end": v(-183.16, 45593) * mm});
            skLineSegment(sketch, "E98.0.11.10", {"start": v(-310.16, 45593) * mm, "end": v(-183.16, 45593) * mm});
            skLineSegment(sketch, "E98.0.11.11", {"start": v(-310.16, 45847) * mm, "end": v(-183.16, 45847) * mm});
            skLineSegment(sketch, "E98.0.11.12", {"start": v(183.16, 45789.85) * mm, "end": v(183.16, 45847) * mm});
            skLineSegment(sketch, "E98.0.11.13", {"start": v(183.16, 45847) * mm, "end": v(310.16, 45847) * mm});
            skLineSegment(sketch, "E98.0.11.14", {"start": v(310.16, 45593) * mm, "end": v(183.16, 45593) * mm});
            skPoint(sketch, "E98.0.12.0", {"position": v(-415.13, 49530) * mm});
            skLineSegment(sketch, "E98.0.12.1", {"start": v(183.16, 49460.15) * mm, "end": v(-183.16, 49460.15) * mm});
            skPoint(sketch, "E98.0.12.2", {"position": v(-310.16, 49530) * mm});
            skPoint(sketch, "E98.0.12.3", {"position": v(0, 49460.15) * mm});
            skLineSegment(sketch, "E98.0.12.4", {"start": v(310.16, 49657) * mm, "end": v(310.16, 49403) * mm});
            skLineSegment(sketch, "E98.0.12.5", {"start": v(-183.16, 49599.85) * mm, "end": v(183.16, 49599.85) * mm});
            skLineSegment(sketch, "E98.0.12.6", {"start": v(-310.16, 49657) * mm, "end": v(-310.16, 49403) * mm});
            skLineSegment(sketch, "E98.0.12.7", {"start": v(-183.16, 49657) * mm, "end": v(-183.16, 49599.85) * mm});
            skLineSegment(sketch, "E98.0.12.8", {"start": v(183.16, 49403) * mm, "end": v(183.16, 49460.15) * mm});
            skLineSegment(sketch, "E98.0.12.9", {"start": v(-183.16, 49460.15) * mm, "end": v(-183.16, 49403) * mm});
            skLineSegment(sketch, "E98.0.12.10", {"start": v(-310.16, 49403) * mm, "end": v(-183.16, 49403) * mm});
            skLineSegment(sketch, "E98.0.12.11", {"start": v(-310.16, 49657) * mm, "end": v(-183.16, 49657) * mm});
            skLineSegment(sketch, "E98.0.12.12", {"start": v(183.16, 49599.85) * mm, "end": v(183.16, 49657) * mm});
            skLineSegment(sketch, "E98.0.12.13", {"start": v(183.16, 49657) * mm, "end": v(310.16, 49657) * mm});
            skLineSegment(sketch, "E98.0.12.14", {"start": v(310.16, 49403) * mm, "end": v(183.16, 49403) * mm});
            skPoint(sketch, "E98.0.13.0", {"position": v(-415.13, 53340) * mm});
            skLineSegment(sketch, "E98.0.13.1", {"start": v(183.16, 53270.15) * mm, "end": v(-183.16, 53270.15) * mm});
            skPoint(sketch, "E98.0.13.2", {"position": v(-310.16, 53340) * mm});
            skPoint(sketch, "E98.0.13.3", {"position": v(0, 53270.15) * mm});
            skLineSegment(sketch, "E98.0.13.4", {"start": v(310.16, 53467) * mm, "end": v(310.16, 53213) * mm});
            skLineSegment(sketch, "E98.0.13.5", {"start": v(-183.16, 53409.85) * mm, "end": v(183.16, 53409.85) * mm});
            skLineSegment(sketch, "E98.0.13.6", {"start": v(-310.16, 53467) * mm, "end": v(-310.16, 53213) * mm});
            skLineSegment(sketch, "E98.0.13.7", {"start": v(-183.16, 53467) * mm, "end": v(-183.16, 53409.85) * mm});
            skLineSegment(sketch, "E98.0.13.8", {"start": v(183.16, 53213) * mm, "end": v(183.16, 53270.15) * mm});
            skLineSegment(sketch, "E98.0.13.9", {"start": v(-183.16, 53270.15) * mm, "end": v(-183.16, 53213) * mm});
            skLineSegment(sketch, "E98.0.13.10", {"start": v(-310.16, 53213) * mm, "end": v(-183.16, 53213) * mm});
            skLineSegment(sketch, "E98.0.13.11", {"start": v(-310.16, 53467) * mm, "end": v(-183.16, 53467) * mm});
            skLineSegment(sketch, "E98.0.13.12", {"start": v(183.16, 53409.85) * mm, "end": v(183.16, 53467) * mm});
            skLineSegment(sketch, "E98.0.13.13", {"start": v(183.16, 53467) * mm, "end": v(310.16, 53467) * mm});
            skLineSegment(sketch, "E98.0.13.14", {"start": v(310.16, 53213) * mm, "end": v(183.16, 53213) * mm});
            skLineSegment(sketch, "E98.direction1", {"start": v(-310.16, 3683) * mm, "end": v(-284.76, 3683) * mm, "construction": true});
            skLineSegment(sketch, "E98.direction2", {"start": v(-310.16, 3683) * mm, "end": v(-310.16, 7493) * mm, "construction": true});
            skLineSegment(sketch, "E99", {"start": v(-2394.92, 0) * mm, "end": v(2520.62, 0) * mm, "construction": true});
            skLineSegment(sketch, "E100.MirrorCS", {"start": v(-310.16, -3937) * mm, "end": v(-183.16, -3937) * mm});
            skLineSegment(sketch, "E101.MirrorCS", {"start": v(-310.16, -3683) * mm, "end": v(-183.16, -3683) * mm});
            skLineSegment(sketch, "E102.MirrorCS", {"start": v(-310.16, -3937) * mm, "end": v(-310.16, -3683) * mm});
            skLineSegment(sketch, "E103.MirrorCS", {"start": v(183.16, -3879.85) * mm, "end": v(183.16, -3937) * mm});
            skLineSegment(sketch, "E104.MirrorCS", {"start": v(-183.16, -3937) * mm, "end": v(-183.16, -3879.85) * mm});
            skLineSegment(sketch, "E105.MirrorCS", {"start": v(310.16, -3937) * mm, "end": v(310.16, -3683) * mm});
            skLineSegment(sketch, "E106.MirrorCS", {"start": v(-183.16, -3879.85) * mm, "end": v(183.16, -3879.85) * mm});
            skLineSegment(sketch, "E107.MirrorCS", {"start": v(-310.16, -30607) * mm, "end": v(-310.16, -30353) * mm});
            skLineSegment(sketch, "E108.MirrorCS", {"start": v(-183.16, -3740.15) * mm, "end": v(-183.16, -3683) * mm});
            skLineSegment(sketch, "E109.MirrorCS", {"start": v(183.16, -3683) * mm, "end": v(183.16, -3740.15) * mm});
            skLineSegment(sketch, "E110.MirrorCS", {"start": v(183.16, -3937) * mm, "end": v(310.16, -3937) * mm});
            skLineSegment(sketch, "E111.MirrorCS", {"start": v(-183.16, -7747) * mm, "end": v(-183.16, -7689.85) * mm});
            skLineSegment(sketch, "E112.MirrorCS", {"start": v(310.16, -22987) * mm, "end": v(310.16, -22733) * mm});
            skLineSegment(sketch, "E113.MirrorCS", {"start": v(-183.16, -30607) * mm, "end": v(-183.16, -30549.85) * mm});
            skLineSegment(sketch, "E114.MirrorCS", {"start": v(183.16, -3740.15) * mm, "end": v(-183.16, -3740.15) * mm});
            skLineSegment(sketch, "E115.MirrorCS", {"start": v(310.16, -3683) * mm, "end": v(183.16, -3683) * mm});
            skLineSegment(sketch, "E116.MirrorCS", {"start": v(-183.16, -7550.15) * mm, "end": v(-183.16, -7493) * mm});
            skLineSegment(sketch, "E117.MirrorCS", {"start": v(-310.16, -22987) * mm, "end": v(-310.16, -22733) * mm});
            skLineSegment(sketch, "E118.MirrorCS", {"start": v(183.16, -22790.15) * mm, "end": v(-183.16, -22790.15) * mm});
            skLineSegment(sketch, "E119.MirrorCS", {"start": v(-183.16, -30410.15) * mm, "end": v(-183.16, -30353) * mm});
            skLineSegment(sketch, "E120.MirrorCS", {"start": v(-310.16, -3683) * mm, "end": v(-284.76, -3683) * mm, "construction": true});
            skLineSegment(sketch, "E121.MirrorCS", {"start": v(183.16, -11360.15) * mm, "end": v(-183.16, -11360.15) * mm});
            skLineSegment(sketch, "E122.MirrorCS", {"start": v(-310.16, -7493) * mm, "end": v(-183.16, -7493) * mm});
            skLineSegment(sketch, "E123.MirrorCS", {"start": v(183.16, -7493) * mm, "end": v(183.16, -7550.15) * mm});
            skLineSegment(sketch, "E124.MirrorCS", {"start": v(-183.16, -22987) * mm, "end": v(-183.16, -22929.85) * mm});
            skLineSegment(sketch, "E125.MirrorCS", {"start": v(183.16, -15309.85) * mm, "end": v(183.16, -15367) * mm});
            skLineSegment(sketch, "E126.MirrorCS", {"start": v(-183.16, -22929.85) * mm, "end": v(183.16, -22929.85) * mm});
            skLineSegment(sketch, "E127.MirrorCS", {"start": v(183.16, -38030.15) * mm, "end": v(-183.16, -38030.15) * mm});
            skLineSegment(sketch, "E128.MirrorCS", {"start": v(-310.16, -30353) * mm, "end": v(-183.16, -30353) * mm});
            skLineSegment(sketch, "E129.MirrorCS", {"start": v(-183.16, -11499.85) * mm, "end": v(183.16, -11499.85) * mm});
            skLineSegment(sketch, "E130.MirrorCS", {"start": v(183.16, -30353) * mm, "end": v(183.16, -30410.15) * mm});
            skLineSegment(sketch, "E131.MirrorCS", {"start": v(183.16, -41840.15) * mm, "end": v(-183.16, -41840.15) * mm});
            skLineSegment(sketch, "E132.MirrorCS", {"start": v(-183.16, -15367) * mm, "end": v(-183.16, -15309.85) * mm});
            skLineSegment(sketch, "E133.MirrorCS", {"start": v(183.16, -26600.15) * mm, "end": v(-183.16, -26600.15) * mm});
            skLineSegment(sketch, "E134.MirrorCS", {"start": v(310.16, -53213) * mm, "end": v(183.16, -53213) * mm});
            skLineSegment(sketch, "E135.MirrorCS", {"start": v(-310.16, -45847) * mm, "end": v(-310.16, -45593) * mm});
            skLineSegment(sketch, "E136.MirrorCS", {"start": v(183.16, -7689.85) * mm, "end": v(183.16, -7747) * mm});
            skLineSegment(sketch, "E137.MirrorCS", {"start": v(-310.16, -7747) * mm, "end": v(-183.16, -7747) * mm});
            skLineSegment(sketch, "E138.MirrorCS", {"start": v(-183.16, -22790.15) * mm, "end": v(-183.16, -22733) * mm});
            skLineSegment(sketch, "E139.MirrorCS", {"start": v(183.16, -22733) * mm, "end": v(183.16, -22790.15) * mm});
            skLineSegment(sketch, "E140.MirrorCS", {"start": v(-310.16, -53467) * mm, "end": v(-310.16, -53213) * mm});
            skLineSegment(sketch, "E141.MirrorCS", {"start": v(-310.16, -38227) * mm, "end": v(-310.16, -37973) * mm});
            skLineSegment(sketch, "E142.MirrorCS", {"start": v(183.16, -15367) * mm, "end": v(310.16, -15367) * mm});
            skLineSegment(sketch, "E143.MirrorCS", {"start": v(183.16, -30549.85) * mm, "end": v(183.16, -30607) * mm});
            skLineSegment(sketch, "E144.MirrorCS", {"start": v(183.16, -11303) * mm, "end": v(183.16, -11360.15) * mm});
            skLineSegment(sketch, "E145.MirrorCS", {"start": v(-183.16, -53409.85) * mm, "end": v(183.16, -53409.85) * mm});
            skLineSegment(sketch, "E146.MirrorCS", {"start": v(-183.16, -38169.85) * mm, "end": v(183.16, -38169.85) * mm});
            skLineSegment(sketch, "E147.MirrorCS", {"start": v(-183.16, -42037) * mm, "end": v(-183.16, -41979.85) * mm});
            skLineSegment(sketch, "E148.MirrorCS", {"start": v(-310.16, -15367) * mm, "end": v(-183.16, -15367) * mm});
            skLineSegment(sketch, "E149.MirrorCS", {"start": v(-310.16, -30607) * mm, "end": v(-183.16, -30607) * mm});
            skLineSegment(sketch, "E150.MirrorCS", {"start": v(310.16, -53467) * mm, "end": v(310.16, -53213) * mm});
            skLineSegment(sketch, "E151.MirrorCS", {"start": v(-310.16, -42037) * mm, "end": v(-310.16, -41783) * mm});
            skLineSegment(sketch, "E152.MirrorCS", {"start": v(-310.16, -26797) * mm, "end": v(-310.16, -26543) * mm});
            skLineSegment(sketch, "E153.MirrorCS", {"start": v(-310.16, -11557) * mm, "end": v(-310.16, -11303) * mm});
            skLineSegment(sketch, "E154.MirrorCS", {"start": v(-183.16, -41979.85) * mm, "end": v(183.16, -41979.85) * mm});
            skLineSegment(sketch, "E155.MirrorCS", {"start": v(-183.16, -45650.15) * mm, "end": v(-183.16, -45593) * mm});
            skLineSegment(sketch, "E156.MirrorCS", {"start": v(-183.16, -26739.85) * mm, "end": v(183.16, -26739.85) * mm});
            skLineSegment(sketch, "E157.MirrorCS", {"start": v(310.16, -42037) * mm, "end": v(310.16, -41783) * mm});
            skLineSegment(sketch, "E158.MirrorCS", {"start": v(183.16, -15113) * mm, "end": v(183.16, -15170.15) * mm});
            skLineSegment(sketch, "E159.MirrorCS", {"start": v(310.16, -26797) * mm, "end": v(310.16, -26543) * mm});
            skLineSegment(sketch, "E160.MirrorCS", {"start": v(310.16, -11557) * mm, "end": v(310.16, -11303) * mm});
            skLineSegment(sketch, "E161.MirrorCS", {"start": v(-183.16, -45847) * mm, "end": v(-183.16, -45789.85) * mm});
            skLineSegment(sketch, "E162.MirrorCS", {"start": v(-310.16, -34163) * mm, "end": v(-183.16, -34163) * mm});
            skLineSegment(sketch, "E163.MirrorCS", {"start": v(310.16, -37973) * mm, "end": v(183.16, -37973) * mm});
            skLineSegment(sketch, "E164.MirrorCS", {"start": v(-310.16, -49403) * mm, "end": v(-183.16, -49403) * mm});
            skLineSegment(sketch, "E165.MirrorCS", {"start": v(-310.16, -15367) * mm, "end": v(-310.16, -15113) * mm});
            skLineSegment(sketch, "E166.MirrorCS", {"start": v(-310.16, -18923) * mm, "end": v(-183.16, -18923) * mm});
            skLineSegment(sketch, "E167.MirrorCS", {"start": v(-310.16, -7747) * mm, "end": v(-310.16, -7493) * mm});
            skLineSegment(sketch, "E168.MirrorCS", {"start": v(-183.16, -7689.85) * mm, "end": v(183.16, -7689.85) * mm});
            skLineSegment(sketch, "E169.MirrorCS", {"start": v(183.16, -53409.85) * mm, "end": v(183.16, -53467) * mm});
            skLineSegment(sketch, "E170.MirrorCS", {"start": v(183.16, -22929.85) * mm, "end": v(183.16, -22987) * mm});
            skLineSegment(sketch, "E171.MirrorCS", {"start": v(310.16, -30607) * mm, "end": v(310.16, -30353) * mm});
            skLineSegment(sketch, "E172.MirrorCS", {"start": v(183.16, -30410.15) * mm, "end": v(-183.16, -30410.15) * mm});
            skLineSegment(sketch, "E173.MirrorCS", {"start": v(183.16, -15170.15) * mm, "end": v(-183.16, -15170.15) * mm});
            skLineSegment(sketch, "E174.MirrorCS", {"start": v(-310.16, -22733) * mm, "end": v(-183.16, -22733) * mm});
            skLineSegment(sketch, "E175.MirrorCS", {"start": v(-183.16, -53270.15) * mm, "end": v(-183.16, -53213) * mm});
            skLineSegment(sketch, "E176.MirrorCS", {"start": v(-183.16, -38030.15) * mm, "end": v(-183.16, -37973) * mm});
            skLineSegment(sketch, "E177.MirrorCS", {"start": v(183.16, -41979.85) * mm, "end": v(183.16, -42037) * mm});
            skLineSegment(sketch, "E178.MirrorCS", {"start": v(183.16, -26739.85) * mm, "end": v(183.16, -26797) * mm});
            skLineSegment(sketch, "E179.MirrorCS", {"start": v(183.16, -37973) * mm, "end": v(183.16, -38030.15) * mm});
            skLineSegment(sketch, "E180.MirrorCS", {"start": v(183.16, -11499.85) * mm, "end": v(183.16, -11557) * mm});
            skLineSegment(sketch, "E181.MirrorCS", {"start": v(-183.16, -53467) * mm, "end": v(-183.16, -53409.85) * mm});
            skLineSegment(sketch, "E182.MirrorCS", {"start": v(-183.16, -38227) * mm, "end": v(-183.16, -38169.85) * mm});
            skLineSegment(sketch, "E183.MirrorCS", {"start": v(310.16, -15113) * mm, "end": v(183.16, -15113) * mm});
            skLineSegment(sketch, "E184.MirrorCS", {"start": v(-183.16, -26600.15) * mm, "end": v(-183.16, -26543) * mm});
            skLineSegment(sketch, "E185.MirrorCS", {"start": v(-183.16, -11360.15) * mm, "end": v(-183.16, -11303) * mm});
            skLineSegment(sketch, "E186.MirrorCS", {"start": v(183.16, -41783) * mm, "end": v(183.16, -41840.15) * mm});
            skLineSegment(sketch, "E187.MirrorCS", {"start": v(183.16, -26543) * mm, "end": v(183.16, -26600.15) * mm});
            skLineSegment(sketch, "E188.MirrorCS", {"start": v(-183.16, -41840.15) * mm, "end": v(-183.16, -41783) * mm});
            skLineSegment(sketch, "E189.MirrorCS", {"start": v(183.16, -30607) * mm, "end": v(310.16, -30607) * mm});
            skLineSegment(sketch, "E190.MirrorCS", {"start": v(183.16, -53270.15) * mm, "end": v(-183.16, -53270.15) * mm});
            skLineSegment(sketch, "E191.MirrorCS", {"start": v(-183.16, -26797) * mm, "end": v(-183.16, -26739.85) * mm});
            skLineSegment(sketch, "E192.MirrorCS", {"start": v(-183.16, -11557) * mm, "end": v(-183.16, -11499.85) * mm});
            skLineSegment(sketch, "E193.MirrorCS", {"start": v(310.16, -38227) * mm, "end": v(310.16, -37973) * mm});
            skLineSegment(sketch, "E194.MirrorCS", {"start": v(-310.16, -45593) * mm, "end": v(-183.16, -45593) * mm});
            skLineSegment(sketch, "E195.MirrorCS", {"start": v(-183.16, -15170.15) * mm, "end": v(-183.16, -15113) * mm});
            skLineSegment(sketch, "E196.MirrorCS", {"start": v(183.16, -34359.85) * mm, "end": v(183.16, -34417) * mm});
            skLineSegment(sketch, "E197.MirrorCS", {"start": v(183.16, -45593) * mm, "end": v(183.16, -45650.15) * mm});
            skLineSegment(sketch, "E198.MirrorCS", {"start": v(183.16, -49599.85) * mm, "end": v(183.16, -49657) * mm});
            skLineSegment(sketch, "E199.MirrorCS", {"start": v(183.16, -19119.85) * mm, "end": v(183.16, -19177) * mm});
            skLineSegment(sketch, "E200.MirrorCS", {"start": v(-310.16, -34417) * mm, "end": v(-183.16, -34417) * mm});
            skLineSegment(sketch, "E201.MirrorCS", {"start": v(-310.16, -49657) * mm, "end": v(-183.16, -49657) * mm});
            skLineSegment(sketch, "E202.MirrorCS", {"start": v(-310.16, -19177) * mm, "end": v(-183.16, -19177) * mm});
            skLineSegment(sketch, "E203.MirrorCS", {"start": v(310.16, -22733) * mm, "end": v(183.16, -22733) * mm});
            skLineSegment(sketch, "E204.MirrorCS", {"start": v(310.16, -7493) * mm, "end": v(183.16, -7493) * mm});
            skLineSegment(sketch, "E205.MirrorCS", {"start": v(183.16, -7550.15) * mm, "end": v(-183.16, -7550.15) * mm});
            skLineSegment(sketch, "E206.MirrorCS", {"start": v(310.16, -7747) * mm, "end": v(310.16, -7493) * mm});
            skLineSegment(sketch, "E207.MirrorCS", {"start": v(183.16, -53467) * mm, "end": v(310.16, -53467) * mm});
            skLineSegment(sketch, "E208.MirrorCS", {"start": v(183.16, -22987) * mm, "end": v(310.16, -22987) * mm});
            skLineSegment(sketch, "E209.MirrorCS", {"start": v(-183.16, -30549.85) * mm, "end": v(183.16, -30549.85) * mm});
            skLineSegment(sketch, "E210.MirrorCS", {"start": v(183.16, -38227) * mm, "end": v(310.16, -38227) * mm});
            skLineSegment(sketch, "E211.MirrorCS", {"start": v(183.16, -7747) * mm, "end": v(310.16, -7747) * mm});
            skLineSegment(sketch, "E212.MirrorCS", {"start": v(-183.16, -15309.85) * mm, "end": v(183.16, -15309.85) * mm});
            skLineSegment(sketch, "E213.MirrorCS", {"start": v(183.16, -38169.85) * mm, "end": v(183.16, -38227) * mm});
            skLineSegment(sketch, "E214.MirrorCS", {"start": v(310.16, -15367) * mm, "end": v(310.16, -15113) * mm});
            skLineSegment(sketch, "E215.MirrorCS", {"start": v(-310.16, -53467) * mm, "end": v(-183.16, -53467) * mm});
            skLineSegment(sketch, "E216.MirrorCS", {"start": v(-310.16, -22987) * mm, "end": v(-183.16, -22987) * mm});
            skLineSegment(sketch, "E217.MirrorCS", {"start": v(-310.16, -38227) * mm, "end": v(-183.16, -38227) * mm});
            skLineSegment(sketch, "E218.MirrorCS", {"start": v(310.16, -26543) * mm, "end": v(183.16, -26543) * mm});
            skLineSegment(sketch, "E219.MirrorCS", {"start": v(-310.16, -34417) * mm, "end": v(-310.16, -34163) * mm});
            skLineSegment(sketch, "E220.MirrorCS", {"start": v(-310.16, -37973) * mm, "end": v(-183.16, -37973) * mm});
            skLineSegment(sketch, "E221.MirrorCS", {"start": v(310.16, -11303) * mm, "end": v(183.16, -11303) * mm});
            skLineSegment(sketch, "E222.MirrorCS", {"start": v(-310.16, -19177) * mm, "end": v(-310.16, -18923) * mm});
            skLineSegment(sketch, "E223.MirrorCS", {"start": v(310.16, -41783) * mm, "end": v(183.16, -41783) * mm});
            skLineSegment(sketch, "E224.MirrorCS", {"start": v(-310.16, -49657) * mm, "end": v(-310.16, -49403) * mm});
            skLineSegment(sketch, "E225.MirrorCS", {"start": v(-310.16, -53213) * mm, "end": v(-183.16, -53213) * mm});
            skLineSegment(sketch, "E226.MirrorCS", {"start": v(183.16, -11557) * mm, "end": v(310.16, -11557) * mm});
            skLineSegment(sketch, "E227.MirrorCS", {"start": v(183.16, -42037) * mm, "end": v(310.16, -42037) * mm});
            skLineSegment(sketch, "E228.MirrorCS", {"start": v(183.16, -26797) * mm, "end": v(310.16, -26797) * mm});
            skLineSegment(sketch, "E229.MirrorCS", {"start": v(183.16, -53213) * mm, "end": v(183.16, -53270.15) * mm});
            skLineSegment(sketch, "E230.MirrorCS", {"start": v(-310.16, -42037) * mm, "end": v(-183.16, -42037) * mm});
            skLineSegment(sketch, "E231.MirrorCS", {"start": v(183.16, -49460.15) * mm, "end": v(-183.16, -49460.15) * mm});
            skLineSegment(sketch, "E232.MirrorCS", {"start": v(-310.16, -26797) * mm, "end": v(-183.16, -26797) * mm});
            skLineSegment(sketch, "E233.MirrorCS", {"start": v(183.16, -34220.15) * mm, "end": v(-183.16, -34220.15) * mm});
            skLineSegment(sketch, "E234.MirrorCS", {"start": v(-310.16, -11557) * mm, "end": v(-183.16, -11557) * mm});
            skLineSegment(sketch, "E235.MirrorCS", {"start": v(183.16, -18980.15) * mm, "end": v(-183.16, -18980.15) * mm});
            skLineSegment(sketch, "E236.MirrorCS", {"start": v(-310.16, -41783) * mm, "end": v(-183.16, -41783) * mm});
            skLineSegment(sketch, "E237.MirrorCS", {"start": v(-310.16, -26543) * mm, "end": v(-183.16, -26543) * mm});
            skLineSegment(sketch, "E238.MirrorCS", {"start": v(310.16, -30353) * mm, "end": v(183.16, -30353) * mm});
            skLineSegment(sketch, "E239.MirrorCS", {"start": v(-310.16, -11303) * mm, "end": v(-183.16, -11303) * mm});
            skLineSegment(sketch, "E240.MirrorCS", {"start": v(-310.16, -45847) * mm, "end": v(-183.16, -45847) * mm});
            skLineSegment(sketch, "E241.MirrorCS", {"start": v(183.16, -45789.85) * mm, "end": v(183.16, -45847) * mm});
            skLineSegment(sketch, "E242.MirrorCS", {"start": v(-310.16, -15113) * mm, "end": v(-183.16, -15113) * mm});
            skLineSegment(sketch, "E243.MirrorCS", {"start": v(-310.16, -3683) * mm, "end": v(-310.16, -7493) * mm, "construction": true});
            skLineSegment(sketch, "E244.MirrorCS", {"start": v(183.16, -45650.15) * mm, "end": v(-183.16, -45650.15) * mm});
            skLineSegment(sketch, "E245.MirrorCS", {"start": v(-183.16, -49657) * mm, "end": v(-183.16, -49599.85) * mm});
            skLineSegment(sketch, "E246.MirrorCS", {"start": v(-183.16, -34417) * mm, "end": v(-183.16, -34359.85) * mm});
            skLineSegment(sketch, "E247.MirrorCS", {"start": v(-183.16, -19177) * mm, "end": v(-183.16, -19119.85) * mm});
            skLineSegment(sketch, "E248.MirrorCS", {"start": v(-183.16, -19119.85) * mm, "end": v(183.16, -19119.85) * mm});
            skLineSegment(sketch, "E249.MirrorCS", {"start": v(-183.16, -49599.85) * mm, "end": v(183.16, -49599.85) * mm});
            skLineSegment(sketch, "E250.MirrorCS", {"start": v(-183.16, -34359.85) * mm, "end": v(183.16, -34359.85) * mm});
            skLineSegment(sketch, "E251.MirrorCS", {"start": v(-183.16, -45789.85) * mm, "end": v(183.16, -45789.85) * mm});
            skLineSegment(sketch, "E252.MirrorCS", {"start": v(-183.16, -49460.15) * mm, "end": v(-183.16, -49403) * mm});
            skLineSegment(sketch, "E253.MirrorCS", {"start": v(-183.16, -34220.15) * mm, "end": v(-183.16, -34163) * mm});
            skLineSegment(sketch, "E254.MirrorCS", {"start": v(-183.16, -18980.15) * mm, "end": v(-183.16, -18923) * mm});
            skLineSegment(sketch, "E255.MirrorCS", {"start": v(310.16, -45847) * mm, "end": v(310.16, -45593) * mm});
            skLineSegment(sketch, "E256.MirrorCS", {"start": v(183.16, -49403) * mm, "end": v(183.16, -49460.15) * mm});
            skLineSegment(sketch, "E257.MirrorCS", {"start": v(183.16, -34163) * mm, "end": v(183.16, -34220.15) * mm});
            skLineSegment(sketch, "E258.MirrorCS", {"start": v(183.16, -18923) * mm, "end": v(183.16, -18980.15) * mm});
            skLineSegment(sketch, "E259.MirrorCS", {"start": v(310.16, -49657) * mm, "end": v(310.16, -49403) * mm});
            skLineSegment(sketch, "E260.MirrorCS", {"start": v(310.16, -34417) * mm, "end": v(310.16, -34163) * mm});
            skLineSegment(sketch, "E261.MirrorCS", {"start": v(310.16, -19177) * mm, "end": v(310.16, -18923) * mm});
            skLineSegment(sketch, "E262.MirrorCS", {"start": v(310.16, -45593) * mm, "end": v(183.16, -45593) * mm});
            skLineSegment(sketch, "E263.MirrorCS", {"start": v(183.16, -45847) * mm, "end": v(310.16, -45847) * mm});
            skLineSegment(sketch, "E264.MirrorCS", {"start": v(310.16, -34163) * mm, "end": v(183.16, -34163) * mm});
            skLineSegment(sketch, "E265.MirrorCS", {"start": v(310.16, -49403) * mm, "end": v(183.16, -49403) * mm});
            skLineSegment(sketch, "E266.MirrorCS", {"start": v(310.16, -18923) * mm, "end": v(183.16, -18923) * mm});
            skLineSegment(sketch, "E267.MirrorCS", {"start": v(183.16, -34417) * mm, "end": v(310.16, -34417) * mm});
            skLineSegment(sketch, "E268.MirrorCS", {"start": v(183.16, -49657) * mm, "end": v(310.16, -49657) * mm});
            skLineSegment(sketch, "E269.MirrorCS", {"start": v(183.16, -19177) * mm, "end": v(310.16, -19177) * mm});
            skPoint(sketch, "E270.MirrorP", {"position": v(-415.13, -7620) * mm});
            skPoint(sketch, "E271.MirrorP", {"position": v(-310.16, -3810) * mm});
            skPoint(sketch, "E272.MirrorP", {"position": v(-415.13, -19050) * mm});
            skPoint(sketch, "E273.MirrorP", {"position": v(-415.13, -38100) * mm});
            skPoint(sketch, "E274.MirrorP", {"position": v(-415.13, -15240) * mm});
            skPoint(sketch, "E275.MirrorP", {"position": v(-415.13, -34290) * mm});
            skPoint(sketch, "E276.MirrorP", {"position": v(-415.13, -53340) * mm});
            skPoint(sketch, "E277.MirrorP", {"position": v(-310.16, -30480) * mm});
            skPoint(sketch, "E278.MirrorP", {"position": v(-415.13, -11430) * mm});
            skPoint(sketch, "E279.MirrorP", {"position": v(-310.16, -7620) * mm});
            skPoint(sketch, "E280.MirrorP", {"position": v(-415.13, -49530) * mm});
            skPoint(sketch, "E281.MirrorP", {"position": v(-415.13, -26670) * mm});
            skPoint(sketch, "E282.MirrorP", {"position": v(0, -3175) * mm});
            skPoint(sketch, "E283.MirrorP", {"position": v(-415.13, -45720) * mm});
            skPoint(sketch, "E284.MirrorP", {"position": v(-310.16, -22860) * mm});
            skPoint(sketch, "E285.MirrorP", {"position": v(0, -41840.15) * mm});
            skPoint(sketch, "E286.MirrorP", {"position": v(-415.13, -41910) * mm});
            skPoint(sketch, "E287.MirrorP", {"position": v(-310.16, -19050) * mm});
            skPoint(sketch, "E288.MirrorP", {"position": v(-310.16, -38100) * mm});
            skPoint(sketch, "E289.MirrorP", {"position": v(-310.16, -15240) * mm});
            skPoint(sketch, "E290.MirrorP", {"position": v(-310.16, -34290) * mm});
            skPoint(sketch, "E291.MirrorP", {"position": v(-310.16, -53340) * mm});
            skPoint(sketch, "E292.MirrorP", {"position": v(-310.16, -11430) * mm});
            skPoint(sketch, "E293.MirrorP", {"position": v(0, -49460.15) * mm});
            skPoint(sketch, "E294.MirrorP", {"position": v(0, -7550.15) * mm});
            skPoint(sketch, "E295.MirrorP", {"position": v(-415.13, -30480) * mm});
            skPoint(sketch, "E296.MirrorP", {"position": v(-310.16, -26670) * mm});
            skPoint(sketch, "E297.MirrorP", {"position": v(0, -3740.15) * mm});
            skPoint(sketch, "E298.MirrorP", {"position": v(-310.16, -45720) * mm});
            skPoint(sketch, "E299.MirrorP", {"position": v(0, -22790.15) * mm});
            skPoint(sketch, "E300.MirrorP", {"position": v(-310.16, -41910) * mm});
            skPoint(sketch, "E301.MirrorP", {"position": v(-415.13, -3810) * mm});
            skPoint(sketch, "E302.MirrorP", {"position": v(-415.13, -22860) * mm});
            skPoint(sketch, "E303.MirrorP", {"position": v(0, -18980.15) * mm});
            skPoint(sketch, "E304.MirrorP", {"position": v(0, -38030.15) * mm});
            skPoint(sketch, "E305.MirrorP", {"position": v(0, -15170.15) * mm});
            skPoint(sketch, "E306.MirrorP", {"position": v(0, -34220.15) * mm});
            skPoint(sketch, "E307.MirrorP", {"position": v(0, -53270.15) * mm});
            skPoint(sketch, "E308.MirrorP", {"position": v(0, -11360.15) * mm});
            skPoint(sketch, "E309.MirrorP", {"position": v(0, -30410.15) * mm});
            skPoint(sketch, "E310.MirrorP", {"position": v(-310.16, -49530) * mm});
            skPoint(sketch, "E311.MirrorP", {"position": v(0, -26600.15) * mm});
            skPoint(sketch, "E312.MirrorP", {"position": v(0, -45650.15) * mm});
            skSolve(sketch);
        }
        {
            var Q0;
            Q0 = qSketchRegion(id + "F7", true);
            var Q1;
            Q1=sQuery(id+"F7.wireOp",EDGE,"E84.top");
            var Q2;
            Q2=sQuery(id+"F7.wireOp",EDGE,"E84.left");
            var Q3;
            Q3=sQuery(id+"F7.wireOp",EDGE,"E95");
            var Q4;
            Q4=sQuery(id+"F7.wireOp",EDGE,"E93");
            var Q5;
            Q5=sQuery(id+"F7.wireOp",EDGE,"E92");
            var Q6;
            Q6=sQuery(id+"F7.wireOp",EDGE,"E91");
            var Q7;
            Q7=sQuery(id+"F7.wireOp",EDGE,"E90");
            var Q8;
            Q8=sQuery(id+"F7.wireOp",EDGE,"E89");
            var Q9;
            Q9=sQuery(id+"F7.wireOp",EDGE,"E88");
            var Q10;
            Q10=sQuery(id+"F7.wireOp",EDGE,"E84.bottom");
            var Q11;
            Q11=sQuery(id+"F7.wireOp",EDGE,"E96");
            var Q12;
            Q12=sQuery(id+"F7.wireOp",EDGE,"E94");
            var Q13;
            Q13=sQuery(id+"F7.wireOp",EDGE,"E98.0.3.4");
            var Q14;
            Q14=sQuery(id+"F7.wireOp",EDGE,"E98.0.3.5");
            var Q15;
            Q15=sQuery(id+"F7.wireOp",EDGE,"E98.0.3.10");
            var Q16;
            Q16=sQuery(id+"F7.wireOp",EDGE,"E98.0.5.11");
            var Q17;
            Q17=sQuery(id+"F7.wireOp",EDGE,"E98.0.5.10");
            var Q18;
            Q18=sQuery(id+"F7.wireOp",EDGE,"E98.0.5.8");
            var Q19;
            Q19=sQuery(id+"F7.wireOp",EDGE,"E98.0.3.13");
            var Q20;
            Q20=sQuery(id+"F7.wireOp",EDGE,"E98.0.3.1");
            var Q21;
            Q21=sQuery(id+"F7.wireOp",EDGE,"E98.0.5.13");
            var Q22;
            Q22=sQuery(id+"F7.wireOp",EDGE,"E98.0.3.9");
            var Q23;
            Q23=sQuery(id+"F7.wireOp",EDGE,"E98.0.5.12");
            var Q24;
            Q24=sQuery(id+"F7.wireOp",EDGE,"E98.0.13.11");
            var Q25;
            Q25=sQuery(id+"F7.wireOp",EDGE,"E98.0.5.4");
            var Q26;
            Q26=sQuery(id+"F7.wireOp",EDGE,"E98.0.3.12");
            var Q27;
            Q27=sQuery(id+"F7.wireOp",EDGE,"E98.0.10.11");
            var Q28;
            Q28=sQuery(id+"F7.wireOp",EDGE,"E98.0.5.7");
            var Q29;
            Q29=sQuery(id+"F7.wireOp",EDGE,"E98.0.10.10");
            var Q30;
            Q30=sQuery(id+"F7.wireOp",EDGE,"E98.0.3.14");
            var Q31;
            Q31=sQuery(id+"F7.wireOp",EDGE,"E98.0.3.6");
            var Q32;
            Q32=sQuery(id+"F7.wireOp",EDGE,"E98.0.13.8");
            var Q33;
            Q33=sQuery(id+"F7.wireOp",EDGE,"E98.0.5.9");
            var Q34;
            Q34=sQuery(id+"F7.wireOp",EDGE,"E98.0.10.13");
            var Q35;
            Q35=sQuery(id+"F7.wireOp",EDGE,"E98.0.13.10");
            var Q36;
            Q36=sQuery(id+"F7.wireOp",EDGE,"E98.0.10.14");
            var Q37;
            Q37=sQuery(id+"F7.wireOp",EDGE,"E98.0.13.13");
            var Q38;
            Q38=sQuery(id+"F7.wireOp",EDGE,"E98.0.3.11");
            var Q39;
            Q39=sQuery(id+"F7.wireOp",EDGE,"E98.0.2.11");
            var Q40;
            Q40=sQuery(id+"F7.wireOp",EDGE,"E98.0.10.9");
            var Q41;
            Q41=sQuery(id+"F7.wireOp",EDGE,"E98.0.5.5");
            var Q42;
            Q42=sQuery(id+"F7.wireOp",EDGE,"E98.0.12.7");
            var Q43;
            Q43=sQuery(id+"F7.wireOp",EDGE,"E98.0.10.8");
            var Q44;
            Q44=sQuery(id+"F7.wireOp",EDGE,"E98.0.13.4");
            var Q45;
            Q45=sQuery(id+"F7.wireOp",EDGE,"E98.0.9.10");
            var Q46;
            Q46=sQuery(id+"F7.wireOp",EDGE,"E98.0.6.11");
            var Q47;
            Q47=sQuery(id+"F7.wireOp",EDGE,"E98.0.13.6");
            var Q48;
            Q48=sQuery(id+"F7.wireOp",EDGE,"E98.0.5.6");
            var Q49;
            Q49=sQuery(id+"F7.wireOp",EDGE,"E98.0.6.10");
            var Q50;
            Q50=sQuery(id+"F7.wireOp",EDGE,"E98.0.2.10");
            var Q51;
            Q51=sQuery(id+"F7.wireOp",EDGE,"E98.0.3.8");
            var Q52;
            Q52=sQuery(id+"F7.wireOp",EDGE,"E98.0.3.7");
            var Q53;
            Q53=sQuery(id+"F7.wireOp",EDGE,"E98.0.5.14");
            var Q54;
            Q54=sQuery(id+"F7.wireOp",EDGE,"E98.0.10.7");
            var Q55;
            Q55=sQuery(id+"F7.wireOp",EDGE,"E98.0.9.8");
            var Q56;
            Q56=sQuery(id+"F7.wireOp",EDGE,"E98.0.10.12");
            var Q57;
            Q57=sQuery(id+"F7.wireOp",EDGE,"E98.0.6.13");
            var Q58;
            Q58=sQuery(id+"F7.wireOp",EDGE,"E98.0.13.9");
            var Q59;
            Q59=sQuery(id+"F7.wireOp",EDGE,"E98.0.12.5");
            var Q60;
            Q60=sQuery(id+"F7.wireOp",EDGE,"E98.0.2.13");
            var Q61;
            Q61=sQuery(id+"F7.wireOp",EDGE,"E98.0.12.6");
            var Q62;
            Q62=sQuery(id+"F7.wireOp",EDGE,"E98.0.2.14");
            var Q63;
            Q63=sQuery(id+"F7.wireOp",EDGE,"E98.0.6.14");
            var Q64;
            Q64=sQuery(id+"F7.wireOp",EDGE,"E98.0.9.11");
            var Q65;
            Q65=sQuery(id+"F7.wireOp",EDGE,"E98.0.13.12");
            var Q66;
            Q66=sQuery(id+"F7.wireOp",EDGE,"E98.0.12.8");
            var Q67;
            Q67=sQuery(id+"F7.wireOp",EDGE,"E98.0.9.13");
            var Q68;
            Q68=sQuery(id+"F7.wireOp",EDGE,"E98.0.12.9");
            var Q69;
            Q69=sQuery(id+"F7.wireOp",EDGE,"E98.0.10.4");
            var Q70;
            Q70=sQuery(id+"F7.wireOp",EDGE,"E98.0.9.7");
            var Q71;
            Q71=sQuery(id+"F7.wireOp",EDGE,"E98.0.7.4");
            var Q72;
            Q72=sQuery(id+"F7.wireOp",EDGE,"E98.0.9.12");
            var Q73;
            Q73=sQuery(id+"F7.wireOp",EDGE,"E98.0.13.5");
            var Q74;
            Q74=sQuery(id+"F7.wireOp",EDGE,"E98.0.9.4");
            var Q75;
            Q75=sQuery(id+"F7.wireOp",EDGE,"E98.0.12.4");
            var Q76;
            Q76=sQuery(id+"F7.wireOp",EDGE,"E98.0.12.1");
            var Q77;
            Q77=sQuery(id+"F7.wireOp",EDGE,"E98.0.13.7");
            var Q78;
            Q78=sQuery(id+"F7.wireOp",EDGE,"E98.0.6.9");
            var Q79;
            Q79=sQuery(id+"F7.wireOp",EDGE,"E98.0.2.9");
            var Q80;
            Q80=sQuery(id+"F7.wireOp",EDGE,"E98.0.6.4");
            var Q81;
            Q81=sQuery(id+"F7.wireOp",EDGE,"E98.0.12.10");
            var Q82;
            Q82=sQuery(id+"F7.wireOp",EDGE,"E98.0.2.12");
            var Q83;
            Q83=sQuery(id+"F7.wireOp",EDGE,"E98.0.6.12");
            var Q84;
            Q84=sQuery(id+"F7.wireOp",EDGE,"E98.0.9.9");
            var Q85;
            Q85=sQuery(id+"F7.wireOp",EDGE,"E98.0.7.1");
            var Q86;
            Q86=sQuery(id+"F7.wireOp",EDGE,"E98.0.7.5");
            var Q87;
            Q87=sQuery(id+"F7.wireOp",EDGE,"E98.0.13.1");
            var Q88;
            Q88=sQuery(id+"F7.wireOp",EDGE,"E98.0.5.1");
            var Q89;
            Q89=sQuery(id+"F7.wireOp",EDGE,"E98.0.6.7");
            var Q90;
            Q90=sQuery(id+"F7.wireOp",EDGE,"E98.0.7.11");
            var Q91;
            Q91=sQuery(id+"F7.wireOp",EDGE,"E98.0.2.7");
            var Q92;
            Q92=sQuery(id+"F7.wireOp",EDGE,"E98.0.10.6");
            var Q93;
            Q93=sQuery(id+"F7.wireOp",EDGE,"E98.0.7.10");
            var Q94;
            Q94=sQuery(id+"F7.wireOp",EDGE,"E98.0.10.5");
            var Q95;
            Q95=sQuery(id+"F7.wireOp",EDGE,"E98.0.12.11");
            var Q96;
            Q96=sQuery(id+"F7.wireOp",EDGE,"E98.0.4.8");
            var Q97;
            Q97=sQuery(id+"F7.wireOp",EDGE,"E98.0.9.5");
            var Q98;
            Q98=sQuery(id+"F7.wireOp",EDGE,"E98.0.8.5");
            var Q99;
            Q99=sQuery(id+"F7.wireOp",EDGE,"E98.0.7.14");
            var Q100;
            Q100=sQuery(id+"F7.wireOp",EDGE,"E98.0.9.6");
            var Q101;
            Q101=sQuery(id+"F7.wireOp",EDGE,"E98.0.7.13");
            var Q102;
            Q102=sQuery(id+"F7.wireOp",EDGE,"E98.0.6.8");
            var Q103;
            Q103=sQuery(id+"F7.wireOp",EDGE,"E98.0.2.8");
            var Q104;
            Q104=sQuery(id+"F7.wireOp",EDGE,"E98.0.10.1");
            var Q105;
            Q105=sQuery(id+"F7.wireOp",EDGE,"E98.0.13.14");
            var Q106;
            Q106=sQuery(id+"F7.wireOp",EDGE,"E98.0.9.1");
            var Q107;
            Q107=sQuery(id+"F7.wireOp",EDGE,"E98.0.4.4");
            var Q108;
            Q108=sQuery(id+"F7.wireOp",EDGE,"E98.0.4.6");
            var Q109;
            Q109=sQuery(id+"F7.wireOp",EDGE,"E98.0.8.6");
            var Q110;
            Q110=sQuery(id+"F7.wireOp",EDGE,"E98.0.4.7");
            var Q111;
            Q111=sQuery(id+"F7.wireOp",EDGE,"E98.0.8.8");
            var Q112;
            Q112=sQuery(id+"F7.wireOp",EDGE,"E98.0.4.9");
            var Q113;
            Q113=sQuery(id+"F7.wireOp",EDGE,"E98.0.8.9");
            var Q114;
            Q114=sQuery(id+"F7.wireOp",EDGE,"E98.0.12.14");
            var Q115;
            Q115=sQuery(id+"F7.wireOp",EDGE,"E98.0.6.6");
            var Q116;
            Q116=sQuery(id+"F7.wireOp",EDGE,"E98.0.2.6");
            var Q117;
            Q117=sQuery(id+"F7.wireOp",EDGE,"E98.0.12.13");
            var Q118;
            Q118=sQuery(id+"F7.wireOp",EDGE,"E98.0.2.4");
            var Q119;
            Q119=sQuery(id+"F7.wireOp",EDGE,"E98.0.7.6");
            var Q120;
            Q120=sQuery(id+"F7.wireOp",EDGE,"E98.0.4.1");
            var Q121;
            Q121=sQuery(id+"F7.wireOp",EDGE,"E98.0.7.12");
            var Q122;
            Q122=sQuery(id+"F7.wireOp",EDGE,"E98.0.8.11");
            var Q123;
            Q123=sQuery(id+"F7.wireOp",EDGE,"E98.0.8.10");
            var Q124;
            Q124=sQuery(id+"F7.wireOp",EDGE,"E98.0.9.14");
            var Q125;
            Q125=sQuery(id+"F7.wireOp",EDGE,"E98.0.4.10");
            var Q126;
            Q126=sQuery(id+"F7.wireOp",EDGE,"E98.0.8.4");
            var Q127;
            Q127=sQuery(id+"F7.wireOp",EDGE,"E98.0.4.5");
            var Q128;
            Q128=sQuery(id+"F7.wireOp",EDGE,"E98.0.8.7");
            var Q129;
            Q129=sQuery(id+"F7.wireOp",EDGE,"E98.0.4.14");
            var Q130;
            Q130=sQuery(id+"F7.wireOp",EDGE,"E98.0.4.13");
            var Q131;
            Q131=sQuery(id+"F7.wireOp",EDGE,"E98.0.6.5");
            var Q132;
            Q132=sQuery(id+"F7.wireOp",EDGE,"E98.0.7.9");
            var Q133;
            Q133=sQuery(id+"F7.wireOp",EDGE,"E98.0.2.5");
            var Q134;
            Q134=sQuery(id+"F7.wireOp",EDGE,"E98.0.12.12");
            var Q135;
            Q135=sQuery(id+"F7.wireOp",EDGE,"E98.0.4.11");
            var Q136;
            Q136=sQuery(id+"F7.wireOp",EDGE,"E98.0.6.1");
            var Q137;
            Q137=sQuery(id+"F7.wireOp",EDGE,"E98.0.2.1");
            var Q138;
            Q138=sQuery(id+"F7.wireOp",EDGE,"E98.0.11.13");
            var Q139;
            Q139=sQuery(id+"F7.wireOp",EDGE,"E98.0.8.1");
            var Q140;
            Q140=sQuery(id+"F7.wireOp",EDGE,"E98.0.4.12");
            var Q141;
            Q141=sQuery(id+"F7.wireOp",EDGE,"E98.0.11.1");
            var Q142;
            Q142=sQuery(id+"F7.wireOp",EDGE,"E98.0.11.5");
            var Q143;
            Q143=sQuery(id+"F7.wireOp",EDGE,"E98.0.8.13");
            var Q144;
            Q144=sQuery(id+"F7.wireOp",EDGE,"E98.0.7.8");
            var Q145;
            Q145=sQuery(id+"F7.wireOp",EDGE,"E98.0.7.7");
            var Q146;
            Q146=sQuery(id+"F7.wireOp",EDGE,"E98.0.11.12");
            var Q147;
            Q147=sQuery(id+"F7.wireOp",EDGE,"E98.0.11.11");
            var Q148;
            Q148=sQuery(id+"F7.wireOp",EDGE,"E98.0.11.4");
            var Q149;
            Q149=sQuery(id+"F7.wireOp",EDGE,"E98.0.8.14");
            var Q150;
            Q150=sQuery(id+"F7.wireOp",EDGE,"E98.0.11.10");
            var Q151;
            Q151=sQuery(id+"F7.wireOp",EDGE,"E98.0.8.12");
            var Q152;
            Q152=sQuery(id+"F7.wireOp",EDGE,"E98.0.11.14");
            var Q153;
            Q153=sQuery(id+"F7.wireOp",EDGE,"E98.0.11.7");
            var Q154;
            Q154=sQuery(id+"F7.wireOp",EDGE,"E98.0.11.9");
            var Q155;
            Q155=sQuery(id+"F7.wireOp",EDGE,"E98.0.11.6");
            var Q156;
            Q156=sQuery(id+"F7.wireOp",EDGE,"E98.0.11.8");
            var Q157;
            Q157=sQuery(id+"F7.wireOp",EDGE,"E98.0.1.6");
            var Q158;
            Q158=sQuery(id+"F7.wireOp",EDGE,"E98.0.1.10");
            var Q159;
            Q159=sQuery(id+"F7.wireOp",EDGE,"E98.0.1.11");
            var Q160;
            Q160=sQuery(id+"F7.wireOp",EDGE,"E98.0.1.7");
            var Q161;
            Q161=sQuery(id+"F7.wireOp",EDGE,"E98.0.1.9");
            var Q162;
            Q162=sQuery(id+"F7.wireOp",EDGE,"E98.0.1.5");
            var Q163;
            Q163=sQuery(id+"F7.wireOp",EDGE,"E98.0.1.1");
            var Q164;
            Q164=sQuery(id+"F7.wireOp",EDGE,"E98.0.1.8");
            var Q165;
            Q165=sQuery(id+"F7.wireOp",EDGE,"E98.0.1.14");
            var Q166;
            Q166=sQuery(id+"F7.wireOp",EDGE,"E98.0.1.4");
            var Q167;
            Q167=sQuery(id+"F7.wireOp",EDGE,"E98.0.1.13");
            var Q168;
            Q168=sQuery(id+"F7.wireOp",EDGE,"E98.0.1.12");
            var Q169;
            Q169=makeQuery(id+"F2.opSweep","SWEPT_BODY",BODY,{"disambiguationData":[OSD([sQuery(id+"F0.wireOp",EDGE,"E0"),sQuery(id+"F0.wireOp",EDGE,"E1"),sQuery(id+"F0.wireOp",EDGE,"E2"),sQuery(id+"F0.wireOp",EDGE,"E3"),sQuery(id+"F0.wireOp",EDGE,"E6.MirrorCS"),sQuery(id+"F0.wireOp",EDGE,"E7.MirrorCS"),sQuery(id+"F0.wireOp",EDGE,"E8.MirrorCS"),sQuery(id+"F0.wireOp",EDGE,"E9"),sQuery(id+"F0.wireOp",EDGE,"E10"),sQuery(id+"F0.wireOp",EDGE,"E11"),sQuery(id+"F0.wireOp",EDGE,"E12"),sQuery(id+"F0.wireOp",EDGE,"E13.MirrorCS"),sQuery(id+"F0.wireOp",EDGE,"E14.MirrorCS"),sQuery(id+"F0.wireOp",EDGE,"E15.MirrorCS"),sQuery(id+"F0.wireOp",EDGE,"E16.MirrorCS"),sQuery(id+"F0.wireOp",EDGE,"E17"),sQuery(id+"F1.wireOp",EDGE,"E21")])]});
            extrude(context, id + "F8", {"entities" : qUnion([Q0]), "surfaceEntities" : qUnion([Q1, Q2, Q3, Q4, Q5, Q6, Q7, Q8, Q9, Q10, Q11, Q12, Q13, Q14, Q15, Q16, Q17, Q18, Q19, Q20, Q21, Q22, Q23, Q24, Q25, Q26, Q27, Q28, Q29, Q30, Q31, Q32, Q33, Q34, Q35, Q36, Q37, Q38, Q39, Q40, Q41, Q42, Q43, Q44, Q45, Q46, Q47, Q48, Q49, Q50, Q51, Q52, Q53, Q54, Q55, Q56, Q57, Q58, Q59, Q60, Q61, Q62, Q63, Q64, Q65, Q66, Q67, Q68, Q69, Q70, Q71, Q72, Q73, Q74, Q75, Q76, Q77, Q78, Q79, Q80, Q81, Q82, Q83, Q84, Q85, Q86, Q87, Q88, Q89, Q90, Q91, Q92, Q93, Q94, Q95, Q96, Q97, Q98, Q99, Q100, Q101, Q102, Q103, Q104, Q105, Q106, Q107, Q108, Q109, Q110, Q111, Q112, Q113, Q114, Q115, Q116, Q117, Q118, Q119, Q120, Q121, Q122, Q123, Q124, Q125, Q126, Q127, Q128, Q129, Q130, Q131, Q132, Q133, Q134, Q135, Q136, Q137, Q138, Q139, Q140, Q141, Q142, Q143, Q144, Q145, Q146, Q147, Q148, Q149, Q150, Q151, Q152, Q153, Q154, Q155, Q156, Q157, Q158, Q159, Q160, Q161, Q162, Q163, Q164, Q165, Q166, Q167, Q168]), "endBound" : BoundingType.UP_TO_BODY, "endBoundEntityBody" : qUnion([Q169]), "depth" : 25.4 * mm});
        }
        {
            var Q0;
            Q0=makeQuery(id+"F8.opExtrude","SWEPT_BODY",BODY,{"disambiguationData":[OSD([sQuery(id+"F7.wireOp",EDGE,"E94")])]});
            var Q1;
            Q1=makeQuery(id+"F8.opExtrude","SWEPT_BODY",BODY,{"disambiguationData":[OSD([sQuery(id+"F7.wireOp",EDGE,"E98.0.1.11")])]});
            var Q2;
            Q2=makeQuery(id+"F8.opExtrude","SWEPT_BODY",BODY,{"disambiguationData":[OSD([sQuery(id+"F7.wireOp",EDGE,"E98.0.2.6")])]});
            var Q3;
            Q3=makeQuery(id+"F8.opExtrude","SWEPT_BODY",BODY,{"disambiguationData":[OSD([sQuery(id+"F7.wireOp",EDGE,"E98.0.3.7")])]});
            var Q4;
            Q4=makeQuery(id+"F8.opExtrude","SWEPT_BODY",BODY,{"disambiguationData":[OSD([sQuery(id+"F7.wireOp",EDGE,"E98.0.4.13")])]});
            var Q5;
            Q5=makeQuery(id+"F8.opExtrude","SWEPT_BODY",BODY,{"disambiguationData":[OSD([sQuery(id+"F7.wireOp",EDGE,"E98.0.5.6")])]});
            var Q6;
            Q6=makeQuery(id+"F8.opExtrude","SWEPT_BODY",BODY,{"disambiguationData":[OSD([sQuery(id+"F7.wireOp",EDGE,"E98.0.6.6")])]});
            var Q7;
            Q7=makeQuery(id+"F8.opExtrude","SWEPT_BODY",BODY,{"disambiguationData":[OSD([sQuery(id+"F7.wireOp",EDGE,"E98.0.7.7")])]});
            var Q8;
            Q8=makeQuery(id+"F8.opExtrude","SWEPT_BODY",BODY,{"disambiguationData":[OSD([sQuery(id+"F7.wireOp",EDGE,"E98.0.8.13")])]});
            var Q9;
            Q9=makeQuery(id+"F8.opExtrude","SWEPT_BODY",BODY,{"disambiguationData":[OSD([sQuery(id+"F7.wireOp",EDGE,"E98.0.9.14")])]});
            var Q10;
            Q10=makeQuery(id+"F8.opExtrude","SWEPT_BODY",BODY,{"disambiguationData":[OSD([sQuery(id+"F7.wireOp",EDGE,"E98.0.10.6")])]});
            var Q11;
            Q11=makeQuery(id+"F8.opExtrude","SWEPT_BODY",BODY,{"disambiguationData":[OSD([sQuery(id+"F7.wireOp",EDGE,"E98.0.11.6")])]});
            var Q12;
            Q12=makeQuery(id+"F8.opExtrude","SWEPT_BODY",BODY,{"disambiguationData":[OSD([sQuery(id+"F7.wireOp",EDGE,"E98.0.12.13")])]});
            var Q13;
            Q13=makeQuery(id+"F8.opExtrude","SWEPT_BODY",BODY,{"disambiguationData":[OSD([sQuery(id+"F7.wireOp",EDGE,"E98.0.13.14")])]});
            var Q14;
            Q14=qCreatedBy(makeId("Front.planeOp"),FACE);
            mirror(context, id + "F9", {"entities" : qUnion([Q0, Q1, Q2, Q3, Q4, Q5, Q6, Q7, Q8, Q9, Q10, Q11, Q12, Q13]), "mirrorPlane" : qUnion([Q14])});
        }
    });
